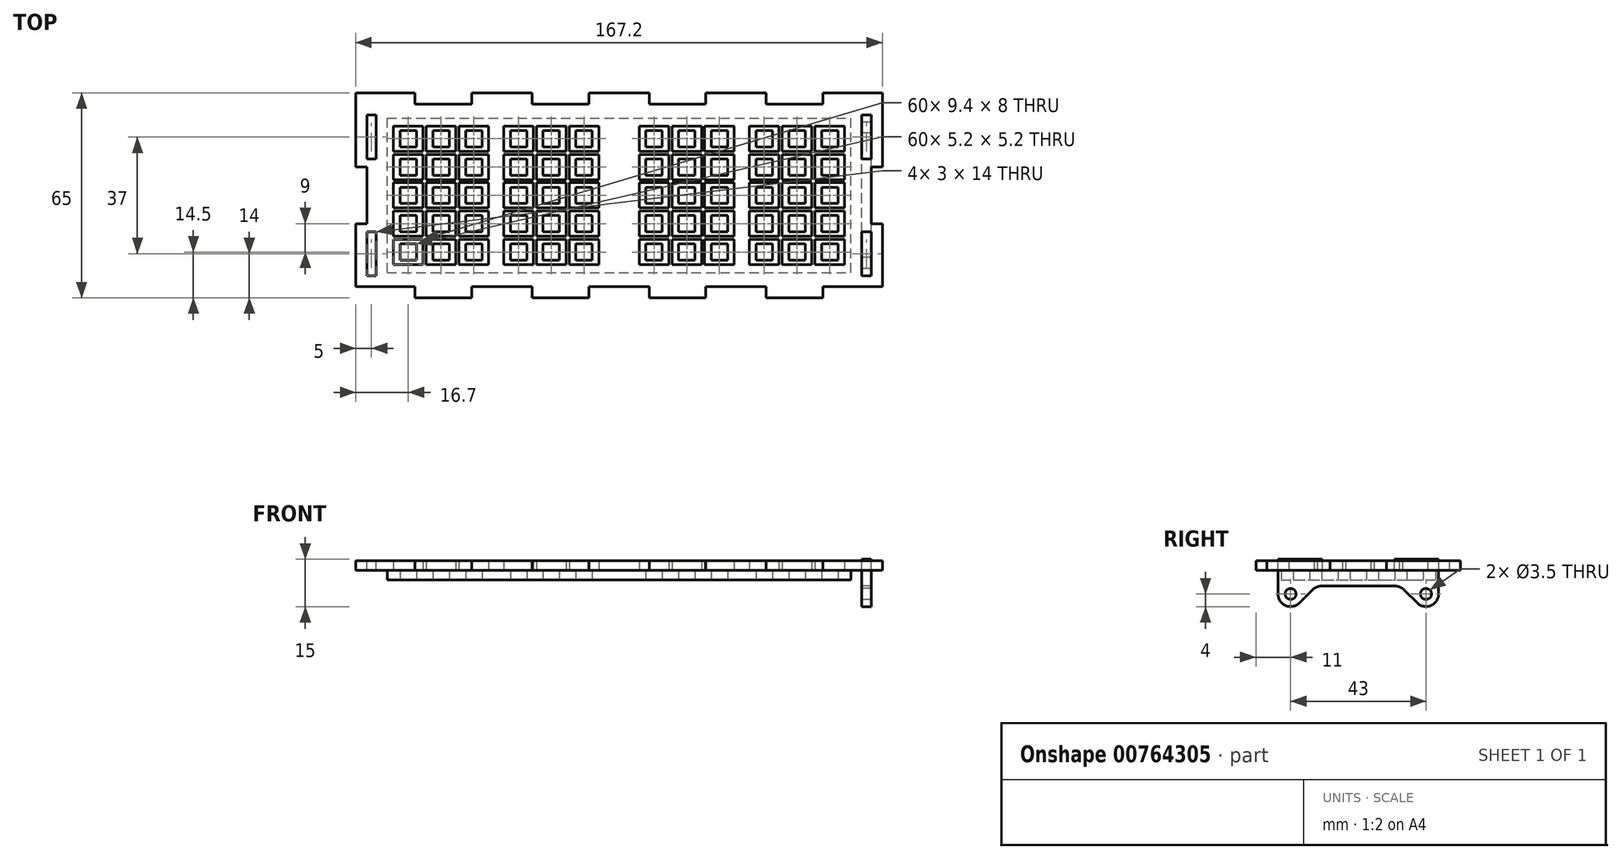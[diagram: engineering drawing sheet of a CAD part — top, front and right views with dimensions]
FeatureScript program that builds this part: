
annotation { "Feature Type Name" : "Feature", "Feature Type Description" : "" }
export const myFeature = defineFeature(function(context is Context, id is Id, definition is map)
    precondition{}
    {
        {
            var Q0;
            Q0=qCreatedBy(makeId("Top.planeOp"),FACE);
            var sketch = newSketch(context, id + "F0", { "sketchPlane" : qUnion([Q0])});
            skLineSegment(sketch, "E0.bottom", {"start": v(0, 0) * mm, "end": v(147.2, 0) * mm});
            skLineSegment(sketch, "E0.left", {"start": v(0, 0) * mm, "end": v(0, 49) * mm});
            skLineSegment(sketch, "E0.right", {"start": v(147.2, 0) * mm, "end": v(147.2, 49) * mm});
            skLineSegment(sketch, "E1.bottom", {"start": v(4.1, 3.9) * mm, "end": v(9.3, 3.9) * mm});
            skLineSegment(sketch, "E1.top", {"start": v(4.1, 9.1) * mm, "end": v(9.3, 9.1) * mm});
            skLineSegment(sketch, "E1.left", {"start": v(4.1, 3.9) * mm, "end": v(4.1, 9.1) * mm});
            skLineSegment(sketch, "E1.right", {"start": v(9.3, 3.9) * mm, "end": v(9.3, 9.1) * mm});
            skLineSegment(sketch, "E2.bottom", {"start": v(39.1, 3.9) * mm, "end": v(44.3, 3.9) * mm});
            skLineSegment(sketch, "E2.top", {"start": v(39.1, 9.1) * mm, "end": v(44.3, 9.1) * mm});
            skLineSegment(sketch, "E2.left", {"start": v(39.1, 3.9) * mm, "end": v(39.1, 9.1) * mm});
            skLineSegment(sketch, "E2.right", {"start": v(44.3, 3.9) * mm, "end": v(44.3, 9.1) * mm});
            skLineSegment(sketch, "E3", {"start": v(0, 49) * mm, "end": v(147.2, 49) * mm});
            skLineSegment(sketch, "E4.bottom", {"start": v(82.1, 3.9) * mm, "end": v(87.3, 3.9) * mm});
            skLineSegment(sketch, "E4.top", {"start": v(82.1, 9.1) * mm, "end": v(87.3, 9.1) * mm});
            skLineSegment(sketch, "E4.left", {"start": v(82.1, 3.9) * mm, "end": v(82.1, 9.1) * mm});
            skLineSegment(sketch, "E4.right", {"start": v(87.3, 3.9) * mm, "end": v(87.3, 9.1) * mm});
            skLineSegment(sketch, "E5.bottom", {"start": v(117.1, 3.9) * mm, "end": v(122.3, 3.9) * mm});
            skLineSegment(sketch, "E5.top", {"start": v(117.1, 9.1) * mm, "end": v(122.3, 9.1) * mm});
            skLineSegment(sketch, "E5.left", {"start": v(117.1, 3.9) * mm, "end": v(117.1, 9.1) * mm});
            skLineSegment(sketch, "E5.right", {"start": v(122.3, 3.9) * mm, "end": v(122.3, 9.1) * mm});
            skLineSegment(sketch, "E6.0.1.0", {"start": v(39.1, 12.9) * mm, "end": v(44.3, 12.9) * mm});
            skLineSegment(sketch, "E6.0.1.1", {"start": v(82.1, 12.9) * mm, "end": v(82.1, 18.1) * mm});
            skLineSegment(sketch, "E6.0.1.2", {"start": v(82.1, 18.1) * mm, "end": v(87.3, 18.1) * mm});
            skLineSegment(sketch, "E6.0.1.3", {"start": v(9.3, 12.9) * mm, "end": v(9.3, 18.1) * mm});
            skLineSegment(sketch, "E6.0.1.4", {"start": v(82.1, 12.9) * mm, "end": v(87.3, 12.9) * mm});
            skLineSegment(sketch, "E6.0.1.5", {"start": v(44.3, 12.9) * mm, "end": v(44.3, 18.1) * mm});
            skLineSegment(sketch, "E6.0.1.6", {"start": v(39.1, 12.9) * mm, "end": v(39.1, 18.1) * mm});
            skLineSegment(sketch, "E6.0.1.7", {"start": v(117.1, 12.9) * mm, "end": v(122.3, 12.9) * mm});
            skLineSegment(sketch, "E6.0.1.8", {"start": v(4.1, 12.9) * mm, "end": v(9.3, 12.9) * mm});
            skLineSegment(sketch, "E6.0.1.9", {"start": v(122.3, 12.9) * mm, "end": v(122.3, 18.1) * mm});
            skLineSegment(sketch, "E6.0.1.10", {"start": v(4.1, 12.9) * mm, "end": v(4.1, 18.1) * mm});
            skLineSegment(sketch, "E6.0.1.11", {"start": v(87.3, 12.9) * mm, "end": v(87.3, 18.1) * mm});
            skLineSegment(sketch, "E6.0.1.12", {"start": v(117.1, 12.9) * mm, "end": v(117.1, 18.1) * mm});
            skLineSegment(sketch, "E6.0.1.13", {"start": v(39.1, 18.1) * mm, "end": v(44.3, 18.1) * mm});
            skLineSegment(sketch, "E6.0.1.14", {"start": v(4.1, 18.1) * mm, "end": v(9.3, 18.1) * mm});
            skLineSegment(sketch, "E6.0.1.15", {"start": v(117.1, 18.1) * mm, "end": v(122.3, 18.1) * mm});
            skLineSegment(sketch, "E6.0.2.0", {"start": v(39.1, 21.9) * mm, "end": v(44.3, 21.9) * mm});
            skLineSegment(sketch, "E6.0.2.1", {"start": v(82.1, 21.9) * mm, "end": v(82.1, 27.1) * mm});
            skLineSegment(sketch, "E6.0.2.2", {"start": v(82.1, 27.1) * mm, "end": v(87.3, 27.1) * mm});
            skLineSegment(sketch, "E6.0.2.3", {"start": v(9.3, 21.9) * mm, "end": v(9.3, 27.1) * mm});
            skLineSegment(sketch, "E6.0.2.4", {"start": v(82.1, 21.9) * mm, "end": v(87.3, 21.9) * mm});
            skLineSegment(sketch, "E6.0.2.5", {"start": v(44.3, 21.9) * mm, "end": v(44.3, 27.1) * mm});
            skLineSegment(sketch, "E6.0.2.6", {"start": v(39.1, 21.9) * mm, "end": v(39.1, 27.1) * mm});
            skLineSegment(sketch, "E6.0.2.7", {"start": v(117.1, 21.9) * mm, "end": v(122.3, 21.9) * mm});
            skLineSegment(sketch, "E6.0.2.8", {"start": v(4.1, 21.9) * mm, "end": v(9.3, 21.9) * mm});
            skLineSegment(sketch, "E6.0.2.9", {"start": v(122.3, 21.9) * mm, "end": v(122.3, 27.1) * mm});
            skLineSegment(sketch, "E6.0.2.10", {"start": v(4.1, 21.9) * mm, "end": v(4.1, 27.1) * mm});
            skLineSegment(sketch, "E6.0.2.11", {"start": v(87.3, 21.9) * mm, "end": v(87.3, 27.1) * mm});
            skLineSegment(sketch, "E6.0.2.12", {"start": v(117.1, 21.9) * mm, "end": v(117.1, 27.1) * mm});
            skLineSegment(sketch, "E6.0.2.13", {"start": v(39.1, 27.1) * mm, "end": v(44.3, 27.1) * mm});
            skLineSegment(sketch, "E6.0.2.14", {"start": v(4.1, 27.1) * mm, "end": v(9.3, 27.1) * mm});
            skLineSegment(sketch, "E6.0.2.15", {"start": v(117.1, 27.1) * mm, "end": v(122.3, 27.1) * mm});
            skLineSegment(sketch, "E6.0.3.0", {"start": v(39.1, 30.9) * mm, "end": v(44.3, 30.9) * mm});
            skLineSegment(sketch, "E6.0.3.1", {"start": v(82.1, 30.9) * mm, "end": v(82.1, 36.1) * mm});
            skLineSegment(sketch, "E6.0.3.2", {"start": v(82.1, 36.1) * mm, "end": v(87.3, 36.1) * mm});
            skLineSegment(sketch, "E6.0.3.3", {"start": v(9.3, 30.9) * mm, "end": v(9.3, 36.1) * mm});
            skLineSegment(sketch, "E6.0.3.4", {"start": v(82.1, 30.9) * mm, "end": v(87.3, 30.9) * mm});
            skLineSegment(sketch, "E6.0.3.5", {"start": v(44.3, 30.9) * mm, "end": v(44.3, 36.1) * mm});
            skLineSegment(sketch, "E6.0.3.6", {"start": v(39.1, 30.9) * mm, "end": v(39.1, 36.1) * mm});
            skLineSegment(sketch, "E6.0.3.7", {"start": v(117.1, 30.9) * mm, "end": v(122.3, 30.9) * mm});
            skLineSegment(sketch, "E6.0.3.8", {"start": v(4.1, 30.9) * mm, "end": v(9.3, 30.9) * mm});
            skLineSegment(sketch, "E6.0.3.9", {"start": v(122.3, 30.9) * mm, "end": v(122.3, 36.1) * mm});
            skLineSegment(sketch, "E6.0.3.10", {"start": v(4.1, 30.9) * mm, "end": v(4.1, 36.1) * mm});
            skLineSegment(sketch, "E6.0.3.11", {"start": v(87.3, 30.9) * mm, "end": v(87.3, 36.1) * mm});
            skLineSegment(sketch, "E6.0.3.12", {"start": v(117.1, 30.9) * mm, "end": v(117.1, 36.1) * mm});
            skLineSegment(sketch, "E6.0.3.13", {"start": v(39.1, 36.1) * mm, "end": v(44.3, 36.1) * mm});
            skLineSegment(sketch, "E6.0.3.14", {"start": v(4.1, 36.1) * mm, "end": v(9.3, 36.1) * mm});
            skLineSegment(sketch, "E6.0.3.15", {"start": v(117.1, 36.1) * mm, "end": v(122.3, 36.1) * mm});
            skLineSegment(sketch, "E6.0.4.0", {"start": v(39.1, 39.9) * mm, "end": v(44.3, 39.9) * mm});
            skLineSegment(sketch, "E6.0.4.1", {"start": v(82.1, 39.9) * mm, "end": v(82.1, 45.1) * mm});
            skLineSegment(sketch, "E6.0.4.2", {"start": v(82.1, 45.1) * mm, "end": v(87.3, 45.1) * mm});
            skLineSegment(sketch, "E6.0.4.3", {"start": v(9.3, 39.9) * mm, "end": v(9.3, 45.1) * mm});
            skLineSegment(sketch, "E6.0.4.4", {"start": v(82.1, 39.9) * mm, "end": v(87.3, 39.9) * mm});
            skLineSegment(sketch, "E6.0.4.5", {"start": v(44.3, 39.9) * mm, "end": v(44.3, 45.1) * mm});
            skLineSegment(sketch, "E6.0.4.6", {"start": v(39.1, 39.9) * mm, "end": v(39.1, 45.1) * mm});
            skLineSegment(sketch, "E6.0.4.7", {"start": v(117.1, 39.9) * mm, "end": v(122.3, 39.9) * mm});
            skLineSegment(sketch, "E6.0.4.8", {"start": v(4.1, 39.9) * mm, "end": v(9.3, 39.9) * mm});
            skLineSegment(sketch, "E6.0.4.9", {"start": v(122.3, 39.9) * mm, "end": v(122.3, 45.1) * mm});
            skLineSegment(sketch, "E6.0.4.10", {"start": v(4.1, 39.9) * mm, "end": v(4.1, 45.1) * mm});
            skLineSegment(sketch, "E6.0.4.11", {"start": v(87.3, 39.9) * mm, "end": v(87.3, 45.1) * mm});
            skLineSegment(sketch, "E6.0.4.12", {"start": v(117.1, 39.9) * mm, "end": v(117.1, 45.1) * mm});
            skLineSegment(sketch, "E6.0.4.13", {"start": v(39.1, 45.1) * mm, "end": v(44.3, 45.1) * mm});
            skLineSegment(sketch, "E6.0.4.14", {"start": v(4.1, 45.1) * mm, "end": v(9.3, 45.1) * mm});
            skLineSegment(sketch, "E6.0.4.15", {"start": v(117.1, 45.1) * mm, "end": v(122.3, 45.1) * mm});
            skLineSegment(sketch, "E6.1.0.0", {"start": v(49.5, 3.9) * mm, "end": v(54.7, 3.9) * mm});
            skLineSegment(sketch, "E6.1.0.1", {"start": v(92.5, 3.9) * mm, "end": v(92.5, 9.1) * mm});
            skLineSegment(sketch, "E6.1.0.2", {"start": v(92.5, 9.1) * mm, "end": v(97.7, 9.1) * mm});
            skLineSegment(sketch, "E6.1.0.3", {"start": v(19.7, 3.9) * mm, "end": v(19.7, 9.1) * mm});
            skLineSegment(sketch, "E6.1.0.4", {"start": v(92.5, 3.9) * mm, "end": v(97.7, 3.9) * mm});
            skLineSegment(sketch, "E6.1.0.5", {"start": v(54.7, 3.9) * mm, "end": v(54.7, 9.1) * mm});
            skLineSegment(sketch, "E6.1.0.6", {"start": v(49.5, 3.9) * mm, "end": v(49.5, 9.1) * mm});
            skLineSegment(sketch, "E6.1.0.7", {"start": v(127.5, 3.9) * mm, "end": v(132.7, 3.9) * mm});
            skLineSegment(sketch, "E6.1.0.8", {"start": v(14.5, 3.9) * mm, "end": v(19.7, 3.9) * mm});
            skLineSegment(sketch, "E6.1.0.9", {"start": v(132.7, 3.9) * mm, "end": v(132.7, 9.1) * mm});
            skLineSegment(sketch, "E6.1.0.10", {"start": v(14.5, 3.9) * mm, "end": v(14.5, 9.1) * mm});
            skLineSegment(sketch, "E6.1.0.11", {"start": v(97.7, 3.9) * mm, "end": v(97.7, 9.1) * mm});
            skLineSegment(sketch, "E6.1.0.12", {"start": v(127.5, 3.9) * mm, "end": v(127.5, 9.1) * mm});
            skLineSegment(sketch, "E6.1.0.13", {"start": v(49.5, 9.1) * mm, "end": v(54.7, 9.1) * mm});
            skLineSegment(sketch, "E6.1.0.14", {"start": v(14.5, 9.1) * mm, "end": v(19.7, 9.1) * mm});
            skLineSegment(sketch, "E6.1.0.15", {"start": v(127.5, 9.1) * mm, "end": v(132.7, 9.1) * mm});
            skLineSegment(sketch, "E6.1.1.0", {"start": v(49.5, 12.9) * mm, "end": v(54.7, 12.9) * mm});
            skLineSegment(sketch, "E6.1.1.1", {"start": v(92.5, 12.9) * mm, "end": v(92.5, 18.1) * mm});
            skLineSegment(sketch, "E6.1.1.2", {"start": v(92.5, 18.1) * mm, "end": v(97.7, 18.1) * mm});
            skLineSegment(sketch, "E6.1.1.3", {"start": v(19.7, 12.9) * mm, "end": v(19.7, 18.1) * mm});
            skLineSegment(sketch, "E6.1.1.4", {"start": v(92.5, 12.9) * mm, "end": v(97.7, 12.9) * mm});
            skLineSegment(sketch, "E6.1.1.5", {"start": v(54.7, 12.9) * mm, "end": v(54.7, 18.1) * mm});
            skLineSegment(sketch, "E6.1.1.6", {"start": v(49.5, 12.9) * mm, "end": v(49.5, 18.1) * mm});
            skLineSegment(sketch, "E6.1.1.7", {"start": v(127.5, 12.9) * mm, "end": v(132.7, 12.9) * mm});
            skLineSegment(sketch, "E6.1.1.8", {"start": v(14.5, 12.9) * mm, "end": v(19.7, 12.9) * mm});
            skLineSegment(sketch, "E6.1.1.9", {"start": v(132.7, 12.9) * mm, "end": v(132.7, 18.1) * mm});
            skLineSegment(sketch, "E6.1.1.10", {"start": v(14.5, 12.9) * mm, "end": v(14.5, 18.1) * mm});
            skLineSegment(sketch, "E6.1.1.11", {"start": v(97.7, 12.9) * mm, "end": v(97.7, 18.1) * mm});
            skLineSegment(sketch, "E6.1.1.12", {"start": v(127.5, 12.9) * mm, "end": v(127.5, 18.1) * mm});
            skLineSegment(sketch, "E6.1.1.13", {"start": v(49.5, 18.1) * mm, "end": v(54.7, 18.1) * mm});
            skLineSegment(sketch, "E6.1.1.14", {"start": v(14.5, 18.1) * mm, "end": v(19.7, 18.1) * mm});
            skLineSegment(sketch, "E6.1.1.15", {"start": v(127.5, 18.1) * mm, "end": v(132.7, 18.1) * mm});
            skLineSegment(sketch, "E6.1.2.0", {"start": v(49.5, 21.9) * mm, "end": v(54.7, 21.9) * mm});
            skLineSegment(sketch, "E6.1.2.1", {"start": v(92.5, 21.9) * mm, "end": v(92.5, 27.1) * mm});
            skLineSegment(sketch, "E6.1.2.2", {"start": v(92.5, 27.1) * mm, "end": v(97.7, 27.1) * mm});
            skLineSegment(sketch, "E6.1.2.3", {"start": v(19.7, 21.9) * mm, "end": v(19.7, 27.1) * mm});
            skLineSegment(sketch, "E6.1.2.4", {"start": v(92.5, 21.9) * mm, "end": v(97.7, 21.9) * mm});
            skLineSegment(sketch, "E6.1.2.5", {"start": v(54.7, 21.9) * mm, "end": v(54.7, 27.1) * mm});
            skLineSegment(sketch, "E6.1.2.6", {"start": v(49.5, 21.9) * mm, "end": v(49.5, 27.1) * mm});
            skLineSegment(sketch, "E6.1.2.7", {"start": v(127.5, 21.9) * mm, "end": v(132.7, 21.9) * mm});
            skLineSegment(sketch, "E6.1.2.8", {"start": v(14.5, 21.9) * mm, "end": v(19.7, 21.9) * mm});
            skLineSegment(sketch, "E6.1.2.9", {"start": v(132.7, 21.9) * mm, "end": v(132.7, 27.1) * mm});
            skLineSegment(sketch, "E6.1.2.10", {"start": v(14.5, 21.9) * mm, "end": v(14.5, 27.1) * mm});
            skLineSegment(sketch, "E6.1.2.11", {"start": v(97.7, 21.9) * mm, "end": v(97.7, 27.1) * mm});
            skLineSegment(sketch, "E6.1.2.12", {"start": v(127.5, 21.9) * mm, "end": v(127.5, 27.1) * mm});
            skLineSegment(sketch, "E6.1.2.13", {"start": v(49.5, 27.1) * mm, "end": v(54.7, 27.1) * mm});
            skLineSegment(sketch, "E6.1.2.14", {"start": v(14.5, 27.1) * mm, "end": v(19.7, 27.1) * mm});
            skLineSegment(sketch, "E6.1.2.15", {"start": v(127.5, 27.1) * mm, "end": v(132.7, 27.1) * mm});
            skLineSegment(sketch, "E6.1.3.0", {"start": v(49.5, 30.9) * mm, "end": v(54.7, 30.9) * mm});
            skLineSegment(sketch, "E6.1.3.1", {"start": v(92.5, 30.9) * mm, "end": v(92.5, 36.1) * mm});
            skLineSegment(sketch, "E6.1.3.2", {"start": v(92.5, 36.1) * mm, "end": v(97.7, 36.1) * mm});
            skLineSegment(sketch, "E6.1.3.3", {"start": v(19.7, 30.9) * mm, "end": v(19.7, 36.1) * mm});
            skLineSegment(sketch, "E6.1.3.4", {"start": v(92.5, 30.9) * mm, "end": v(97.7, 30.9) * mm});
            skLineSegment(sketch, "E6.1.3.5", {"start": v(54.7, 30.9) * mm, "end": v(54.7, 36.1) * mm});
            skLineSegment(sketch, "E6.1.3.6", {"start": v(49.5, 30.9) * mm, "end": v(49.5, 36.1) * mm});
            skLineSegment(sketch, "E6.1.3.7", {"start": v(127.5, 30.9) * mm, "end": v(132.7, 30.9) * mm});
            skLineSegment(sketch, "E6.1.3.8", {"start": v(14.5, 30.9) * mm, "end": v(19.7, 30.9) * mm});
            skLineSegment(sketch, "E6.1.3.9", {"start": v(132.7, 30.9) * mm, "end": v(132.7, 36.1) * mm});
            skLineSegment(sketch, "E6.1.3.10", {"start": v(14.5, 30.9) * mm, "end": v(14.5, 36.1) * mm});
            skLineSegment(sketch, "E6.1.3.11", {"start": v(97.7, 30.9) * mm, "end": v(97.7, 36.1) * mm});
            skLineSegment(sketch, "E6.1.3.12", {"start": v(127.5, 30.9) * mm, "end": v(127.5, 36.1) * mm});
            skLineSegment(sketch, "E6.1.3.13", {"start": v(49.5, 36.1) * mm, "end": v(54.7, 36.1) * mm});
            skLineSegment(sketch, "E6.1.3.14", {"start": v(14.5, 36.1) * mm, "end": v(19.7, 36.1) * mm});
            skLineSegment(sketch, "E6.1.3.15", {"start": v(127.5, 36.1) * mm, "end": v(132.7, 36.1) * mm});
            skLineSegment(sketch, "E6.1.4.0", {"start": v(49.5, 39.9) * mm, "end": v(54.7, 39.9) * mm});
            skLineSegment(sketch, "E6.1.4.1", {"start": v(92.5, 39.9) * mm, "end": v(92.5, 45.1) * mm});
            skLineSegment(sketch, "E6.1.4.2", {"start": v(92.5, 45.1) * mm, "end": v(97.7, 45.1) * mm});
            skLineSegment(sketch, "E6.1.4.3", {"start": v(19.7, 39.9) * mm, "end": v(19.7, 45.1) * mm});
            skLineSegment(sketch, "E6.1.4.4", {"start": v(92.5, 39.9) * mm, "end": v(97.7, 39.9) * mm});
            skLineSegment(sketch, "E6.1.4.5", {"start": v(54.7, 39.9) * mm, "end": v(54.7, 45.1) * mm});
            skLineSegment(sketch, "E6.1.4.6", {"start": v(49.5, 39.9) * mm, "end": v(49.5, 45.1) * mm});
            skLineSegment(sketch, "E6.1.4.7", {"start": v(127.5, 39.9) * mm, "end": v(132.7, 39.9) * mm});
            skLineSegment(sketch, "E6.1.4.8", {"start": v(14.5, 39.9) * mm, "end": v(19.7, 39.9) * mm});
            skLineSegment(sketch, "E6.1.4.9", {"start": v(132.7, 39.9) * mm, "end": v(132.7, 45.1) * mm});
            skLineSegment(sketch, "E6.1.4.10", {"start": v(14.5, 39.9) * mm, "end": v(14.5, 45.1) * mm});
            skLineSegment(sketch, "E6.1.4.11", {"start": v(97.7, 39.9) * mm, "end": v(97.7, 45.1) * mm});
            skLineSegment(sketch, "E6.1.4.12", {"start": v(127.5, 39.9) * mm, "end": v(127.5, 45.1) * mm});
            skLineSegment(sketch, "E6.1.4.13", {"start": v(49.5, 45.1) * mm, "end": v(54.7, 45.1) * mm});
            skLineSegment(sketch, "E6.1.4.14", {"start": v(14.5, 45.1) * mm, "end": v(19.7, 45.1) * mm});
            skLineSegment(sketch, "E6.1.4.15", {"start": v(127.5, 45.1) * mm, "end": v(132.7, 45.1) * mm});
            skLineSegment(sketch, "E6.2.0.0", {"start": v(59.9, 3.9) * mm, "end": v(65.1, 3.9) * mm});
            skLineSegment(sketch, "E6.2.0.1", {"start": v(102.9, 3.9) * mm, "end": v(102.9, 9.1) * mm});
            skLineSegment(sketch, "E6.2.0.2", {"start": v(102.9, 9.1) * mm, "end": v(108.1, 9.1) * mm});
            skLineSegment(sketch, "E6.2.0.3", {"start": v(30.1, 3.9) * mm, "end": v(30.1, 9.1) * mm});
            skLineSegment(sketch, "E6.2.0.4", {"start": v(102.9, 3.9) * mm, "end": v(108.1, 3.9) * mm});
            skLineSegment(sketch, "E6.2.0.5", {"start": v(65.1, 3.9) * mm, "end": v(65.1, 9.1) * mm});
            skLineSegment(sketch, "E6.2.0.6", {"start": v(59.9, 3.9) * mm, "end": v(59.9, 9.1) * mm});
            skLineSegment(sketch, "E6.2.0.7", {"start": v(137.9, 3.9) * mm, "end": v(143.1, 3.9) * mm});
            skLineSegment(sketch, "E6.2.0.8", {"start": v(24.9, 3.9) * mm, "end": v(30.1, 3.9) * mm});
            skLineSegment(sketch, "E6.2.0.9", {"start": v(143.1, 3.9) * mm, "end": v(143.1, 9.1) * mm});
            skLineSegment(sketch, "E6.2.0.10", {"start": v(24.9, 3.9) * mm, "end": v(24.9, 9.1) * mm});
            skLineSegment(sketch, "E6.2.0.11", {"start": v(108.1, 3.9) * mm, "end": v(108.1, 9.1) * mm});
            skLineSegment(sketch, "E6.2.0.12", {"start": v(137.9, 3.9) * mm, "end": v(137.9, 9.1) * mm});
            skLineSegment(sketch, "E6.2.0.13", {"start": v(59.9, 9.1) * mm, "end": v(65.1, 9.1) * mm});
            skLineSegment(sketch, "E6.2.0.14", {"start": v(24.9, 9.1) * mm, "end": v(30.1, 9.1) * mm});
            skLineSegment(sketch, "E6.2.0.15", {"start": v(137.9, 9.1) * mm, "end": v(143.1, 9.1) * mm});
            skLineSegment(sketch, "E6.2.1.0", {"start": v(59.9, 12.9) * mm, "end": v(65.1, 12.9) * mm});
            skLineSegment(sketch, "E6.2.1.1", {"start": v(102.9, 12.9) * mm, "end": v(102.9, 18.1) * mm});
            skLineSegment(sketch, "E6.2.1.2", {"start": v(102.9, 18.1) * mm, "end": v(108.1, 18.1) * mm});
            skLineSegment(sketch, "E6.2.1.3", {"start": v(30.1, 12.9) * mm, "end": v(30.1, 18.1) * mm});
            skLineSegment(sketch, "E6.2.1.4", {"start": v(102.9, 12.9) * mm, "end": v(108.1, 12.9) * mm});
            skLineSegment(sketch, "E6.2.1.5", {"start": v(65.1, 12.9) * mm, "end": v(65.1, 18.1) * mm});
            skLineSegment(sketch, "E6.2.1.6", {"start": v(59.9, 12.9) * mm, "end": v(59.9, 18.1) * mm});
            skLineSegment(sketch, "E6.2.1.7", {"start": v(137.9, 12.9) * mm, "end": v(143.1, 12.9) * mm});
            skLineSegment(sketch, "E6.2.1.8", {"start": v(24.9, 12.9) * mm, "end": v(30.1, 12.9) * mm});
            skLineSegment(sketch, "E6.2.1.9", {"start": v(143.1, 12.9) * mm, "end": v(143.1, 18.1) * mm});
            skLineSegment(sketch, "E6.2.1.10", {"start": v(24.9, 12.9) * mm, "end": v(24.9, 18.1) * mm});
            skLineSegment(sketch, "E6.2.1.11", {"start": v(108.1, 12.9) * mm, "end": v(108.1, 18.1) * mm});
            skLineSegment(sketch, "E6.2.1.12", {"start": v(137.9, 12.9) * mm, "end": v(137.9, 18.1) * mm});
            skLineSegment(sketch, "E6.2.1.13", {"start": v(59.9, 18.1) * mm, "end": v(65.1, 18.1) * mm});
            skLineSegment(sketch, "E6.2.1.14", {"start": v(24.9, 18.1) * mm, "end": v(30.1, 18.1) * mm});
            skLineSegment(sketch, "E6.2.1.15", {"start": v(137.9, 18.1) * mm, "end": v(143.1, 18.1) * mm});
            skLineSegment(sketch, "E6.2.2.0", {"start": v(59.9, 21.9) * mm, "end": v(65.1, 21.9) * mm});
            skLineSegment(sketch, "E6.2.2.1", {"start": v(102.9, 21.9) * mm, "end": v(102.9, 27.1) * mm});
            skLineSegment(sketch, "E6.2.2.2", {"start": v(102.9, 27.1) * mm, "end": v(108.1, 27.1) * mm});
            skLineSegment(sketch, "E6.2.2.3", {"start": v(30.1, 21.9) * mm, "end": v(30.1, 27.1) * mm});
            skLineSegment(sketch, "E6.2.2.4", {"start": v(102.9, 21.9) * mm, "end": v(108.1, 21.9) * mm});
            skLineSegment(sketch, "E6.2.2.5", {"start": v(65.1, 21.9) * mm, "end": v(65.1, 27.1) * mm});
            skLineSegment(sketch, "E6.2.2.6", {"start": v(59.9, 21.9) * mm, "end": v(59.9, 27.1) * mm});
            skLineSegment(sketch, "E6.2.2.7", {"start": v(137.9, 21.9) * mm, "end": v(143.1, 21.9) * mm});
            skLineSegment(sketch, "E6.2.2.8", {"start": v(24.9, 21.9) * mm, "end": v(30.1, 21.9) * mm});
            skLineSegment(sketch, "E6.2.2.9", {"start": v(143.1, 21.9) * mm, "end": v(143.1, 27.1) * mm});
            skLineSegment(sketch, "E6.2.2.10", {"start": v(24.9, 21.9) * mm, "end": v(24.9, 27.1) * mm});
            skLineSegment(sketch, "E6.2.2.11", {"start": v(108.1, 21.9) * mm, "end": v(108.1, 27.1) * mm});
            skLineSegment(sketch, "E6.2.2.12", {"start": v(137.9, 21.9) * mm, "end": v(137.9, 27.1) * mm});
            skLineSegment(sketch, "E6.2.2.13", {"start": v(59.9, 27.1) * mm, "end": v(65.1, 27.1) * mm});
            skLineSegment(sketch, "E6.2.2.14", {"start": v(24.9, 27.1) * mm, "end": v(30.1, 27.1) * mm});
            skLineSegment(sketch, "E6.2.2.15", {"start": v(137.9, 27.1) * mm, "end": v(143.1, 27.1) * mm});
            skLineSegment(sketch, "E6.2.3.0", {"start": v(59.9, 30.9) * mm, "end": v(65.1, 30.9) * mm});
            skLineSegment(sketch, "E6.2.3.1", {"start": v(102.9, 30.9) * mm, "end": v(102.9, 36.1) * mm});
            skLineSegment(sketch, "E6.2.3.2", {"start": v(102.9, 36.1) * mm, "end": v(108.1, 36.1) * mm});
            skLineSegment(sketch, "E6.2.3.3", {"start": v(30.1, 30.9) * mm, "end": v(30.1, 36.1) * mm});
            skLineSegment(sketch, "E6.2.3.4", {"start": v(102.9, 30.9) * mm, "end": v(108.1, 30.9) * mm});
            skLineSegment(sketch, "E6.2.3.5", {"start": v(65.1, 30.9) * mm, "end": v(65.1, 36.1) * mm});
            skLineSegment(sketch, "E6.2.3.6", {"start": v(59.9, 30.9) * mm, "end": v(59.9, 36.1) * mm});
            skLineSegment(sketch, "E6.2.3.7", {"start": v(137.9, 30.9) * mm, "end": v(143.1, 30.9) * mm});
            skLineSegment(sketch, "E6.2.3.8", {"start": v(24.9, 30.9) * mm, "end": v(30.1, 30.9) * mm});
            skLineSegment(sketch, "E6.2.3.9", {"start": v(143.1, 30.9) * mm, "end": v(143.1, 36.1) * mm});
            skLineSegment(sketch, "E6.2.3.10", {"start": v(24.9, 30.9) * mm, "end": v(24.9, 36.1) * mm});
            skLineSegment(sketch, "E6.2.3.11", {"start": v(108.1, 30.9) * mm, "end": v(108.1, 36.1) * mm});
            skLineSegment(sketch, "E6.2.3.12", {"start": v(137.9, 30.9) * mm, "end": v(137.9, 36.1) * mm});
            skLineSegment(sketch, "E6.2.3.13", {"start": v(59.9, 36.1) * mm, "end": v(65.1, 36.1) * mm});
            skLineSegment(sketch, "E6.2.3.14", {"start": v(24.9, 36.1) * mm, "end": v(30.1, 36.1) * mm});
            skLineSegment(sketch, "E6.2.3.15", {"start": v(137.9, 36.1) * mm, "end": v(143.1, 36.1) * mm});
            skLineSegment(sketch, "E6.2.4.0", {"start": v(59.9, 39.9) * mm, "end": v(65.1, 39.9) * mm});
            skLineSegment(sketch, "E6.2.4.1", {"start": v(102.9, 39.9) * mm, "end": v(102.9, 45.1) * mm});
            skLineSegment(sketch, "E6.2.4.2", {"start": v(102.9, 45.1) * mm, "end": v(108.1, 45.1) * mm});
            skLineSegment(sketch, "E6.2.4.3", {"start": v(30.1, 39.9) * mm, "end": v(30.1, 45.1) * mm});
            skLineSegment(sketch, "E6.2.4.4", {"start": v(102.9, 39.9) * mm, "end": v(108.1, 39.9) * mm});
            skLineSegment(sketch, "E6.2.4.5", {"start": v(65.1, 39.9) * mm, "end": v(65.1, 45.1) * mm});
            skLineSegment(sketch, "E6.2.4.6", {"start": v(59.9, 39.9) * mm, "end": v(59.9, 45.1) * mm});
            skLineSegment(sketch, "E6.2.4.7", {"start": v(137.9, 39.9) * mm, "end": v(143.1, 39.9) * mm});
            skLineSegment(sketch, "E6.2.4.8", {"start": v(24.9, 39.9) * mm, "end": v(30.1, 39.9) * mm});
            skLineSegment(sketch, "E6.2.4.9", {"start": v(143.1, 39.9) * mm, "end": v(143.1, 45.1) * mm});
            skLineSegment(sketch, "E6.2.4.10", {"start": v(24.9, 39.9) * mm, "end": v(24.9, 45.1) * mm});
            skLineSegment(sketch, "E6.2.4.11", {"start": v(108.1, 39.9) * mm, "end": v(108.1, 45.1) * mm});
            skLineSegment(sketch, "E6.2.4.12", {"start": v(137.9, 39.9) * mm, "end": v(137.9, 45.1) * mm});
            skLineSegment(sketch, "E6.2.4.13", {"start": v(59.9, 45.1) * mm, "end": v(65.1, 45.1) * mm});
            skLineSegment(sketch, "E6.2.4.14", {"start": v(24.9, 45.1) * mm, "end": v(30.1, 45.1) * mm});
            skLineSegment(sketch, "E6.2.4.15", {"start": v(137.9, 45.1) * mm, "end": v(143.1, 45.1) * mm});
            skLineSegment(sketch, "E6.direction1", {"start": v(4.1, 3.9) * mm, "end": v(14.5, 3.9) * mm, "construction": true});
            skLineSegment(sketch, "E6.direction2", {"start": v(4.1, 3.9) * mm, "end": v(4.1, 12.9) * mm, "construction": true});
            skSolve(sketch);
        }
        {
            var Q0;
            Q0=makeQuery(id+"F0.imprint","IMPRINT",FACE,{"disambiguationData":[TD([[makeQuery(id+"F0.imprint","IMPRINT",EDGE,{"derivedFrom":sQuery(id+"F0.wireOp",EDGE,"E0.bottom")}),1.0]])]});
            extrude(context, id + "F1", {"entities" : qUnion([Q0]), "depth" : 3 * mm, "offsetDistance" : 25 * mm});
        }
        {
            var Q0;
            Q0=makeQuery(id+"F1.opExtrude","CAP_FACE",FACE,{"disambiguationData":[OSD([sQuery(id+"F0.wireOp",EDGE,"E0.bottom"),sQuery(id+"F0.wireOp",EDGE,"E0.top"),sQuery(id+"F0.wireOp",EDGE,"E0.left"),sQuery(id+"F0.wireOp",EDGE,"E0.right"),sQuery(id+"F0.wireOp",EDGE,"E1.bottom"),sQuery(id+"F0.wireOp",EDGE,"E1.top"),sQuery(id+"F0.wireOp",EDGE,"E1.left"),sQuery(id+"F0.wireOp",EDGE,"E1.right"),sQuery(id+"F0.wireOp",EDGE,"95869116-3487-4177-9028-07c310471c4a.0.1.0"),sQuery(id+"F0.wireOp",EDGE,"95869116-3487-4177-9028-07c310471c4a.0.1.1"),sQuery(id+"F0.wireOp",EDGE,"95869116-3487-4177-9028-07c310471c4a.0.1.2"),sQuery(id+"F0.wireOp",EDGE,"95869116-3487-4177-9028-07c310471c4a.0.1.3"),sQuery(id+"F0.wireOp",EDGE,"95869116-3487-4177-9028-07c310471c4a.0.2.0"),sQuery(id+"F0.wireOp",EDGE,"95869116-3487-4177-9028-07c310471c4a.0.2.1"),sQuery(id+"F0.wireOp",EDGE,"95869116-3487-4177-9028-07c310471c4a.0.2.2"),sQuery(id+"F0.wireOp",EDGE,"95869116-3487-4177-9028-07c310471c4a.0.2.3"),sQuery(id+"F0.wireOp",EDGE,"95869116-3487-4177-9028-07c310471c4a.0.3.0"),sQuery(id+"F0.wireOp",EDGE,"95869116-3487-4177-9028-07c310471c4a.0.3.1"),sQuery(id+"F0.wireOp",EDGE,"95869116-3487-4177-9028-07c310471c4a.0.3.2"),sQuery(id+"F0.wireOp",EDGE,"95869116-3487-4177-9028-07c310471c4a.0.3.3"),sQuery(id+"F0.wireOp",EDGE,"95869116-3487-4177-9028-07c310471c4a.0.4.0"),sQuery(id+"F0.wireOp",EDGE,"95869116-3487-4177-9028-07c310471c4a.0.4.1"),sQuery(id+"F0.wireOp",EDGE,"95869116-3487-4177-9028-07c310471c4a.0.4.2"),sQuery(id+"F0.wireOp",EDGE,"95869116-3487-4177-9028-07c310471c4a.0.4.3"),sQuery(id+"F0.wireOp",EDGE,"95869116-3487-4177-9028-07c310471c4a.1.0.0"),sQuery(id+"F0.wireOp",EDGE,"95869116-3487-4177-9028-07c310471c4a.1.0.1"),sQuery(id+"F0.wireOp",EDGE,"95869116-3487-4177-9028-07c310471c4a.1.0.2"),sQuery(id+"F0.wireOp",EDGE,"95869116-3487-4177-9028-07c310471c4a.1.0.3"),sQuery(id+"F0.wireOp",EDGE,"95869116-3487-4177-9028-07c310471c4a.1.1.0"),sQuery(id+"F0.wireOp",EDGE,"95869116-3487-4177-9028-07c310471c4a.1.1.1"),sQuery(id+"F0.wireOp",EDGE,"95869116-3487-4177-9028-07c310471c4a.1.1.2"),sQuery(id+"F0.wireOp",EDGE,"95869116-3487-4177-9028-07c310471c4a.1.1.3"),sQuery(id+"F0.wireOp",EDGE,"95869116-3487-4177-9028-07c310471c4a.1.2.0"),sQuery(id+"F0.wireOp",EDGE,"95869116-3487-4177-9028-07c310471c4a.1.2.1"),sQuery(id+"F0.wireOp",EDGE,"95869116-3487-4177-9028-07c310471c4a.1.2.2"),sQuery(id+"F0.wireOp",EDGE,"95869116-3487-4177-9028-07c310471c4a.1.2.3"),sQuery(id+"F0.wireOp",EDGE,"95869116-3487-4177-9028-07c310471c4a.1.3.0"),sQuery(id+"F0.wireOp",EDGE,"95869116-3487-4177-9028-07c310471c4a.1.3.1"),sQuery(id+"F0.wireOp",EDGE,"95869116-3487-4177-9028-07c310471c4a.1.3.2"),sQuery(id+"F0.wireOp",EDGE,"95869116-3487-4177-9028-07c310471c4a.1.3.3"),sQuery(id+"F0.wireOp",EDGE,"95869116-3487-4177-9028-07c310471c4a.1.4.0"),sQuery(id+"F0.wireOp",EDGE,"95869116-3487-4177-9028-07c310471c4a.1.4.1"),sQuery(id+"F0.wireOp",EDGE,"95869116-3487-4177-9028-07c310471c4a.1.4.2"),sQuery(id+"F0.wireOp",EDGE,"95869116-3487-4177-9028-07c310471c4a.1.4.3"),sQuery(id+"F0.wireOp",EDGE,"95869116-3487-4177-9028-07c310471c4a.2.0.0"),sQuery(id+"F0.wireOp",EDGE,"95869116-3487-4177-9028-07c310471c4a.2.0.1"),sQuery(id+"F0.wireOp",EDGE,"95869116-3487-4177-9028-07c310471c4a.2.0.2"),sQuery(id+"F0.wireOp",EDGE,"95869116-3487-4177-9028-07c310471c4a.2.0.3"),sQuery(id+"F0.wireOp",EDGE,"95869116-3487-4177-9028-07c310471c4a.2.1.0"),sQuery(id+"F0.wireOp",EDGE,"95869116-3487-4177-9028-07c310471c4a.2.1.1"),sQuery(id+"F0.wireOp",EDGE,"95869116-3487-4177-9028-07c310471c4a.2.1.2"),sQuery(id+"F0.wireOp",EDGE,"95869116-3487-4177-9028-07c310471c4a.2.1.3"),sQuery(id+"F0.wireOp",EDGE,"95869116-3487-4177-9028-07c310471c4a.2.2.0"),sQuery(id+"F0.wireOp",EDGE,"95869116-3487-4177-9028-07c310471c4a.2.2.1"),sQuery(id+"F0.wireOp",EDGE,"95869116-3487-4177-9028-07c310471c4a.2.2.2"),sQuery(id+"F0.wireOp",EDGE,"95869116-3487-4177-9028-07c310471c4a.2.2.3"),sQuery(id+"F0.wireOp",EDGE,"95869116-3487-4177-9028-07c310471c4a.2.3.0"),sQuery(id+"F0.wireOp",EDGE,"95869116-3487-4177-9028-07c310471c4a.2.3.1"),sQuery(id+"F0.wireOp",EDGE,"95869116-3487-4177-9028-07c310471c4a.2.3.2"),sQuery(id+"F0.wireOp",EDGE,"95869116-3487-4177-9028-07c310471c4a.2.3.3"),sQuery(id+"F0.wireOp",EDGE,"95869116-3487-4177-9028-07c310471c4a.2.4.0"),sQuery(id+"F0.wireOp",EDGE,"95869116-3487-4177-9028-07c310471c4a.2.4.1"),sQuery(id+"F0.wireOp",EDGE,"95869116-3487-4177-9028-07c310471c4a.2.4.2"),sQuery(id+"F0.wireOp",EDGE,"95869116-3487-4177-9028-07c310471c4a.2.4.3"),sQuery(id+"F0.wireOp",EDGE,"49dafa04-c45d-4b5c-802c-71c5818911b00.MirrorCS"),sQuery(id+"F0.wireOp",EDGE,"49dafa04-c45d-4b5c-802c-71c5818911b01.MirrorCS"),sQuery(id+"F0.wireOp",EDGE,"49dafa04-c45d-4b5c-802c-71c5818911b02.MirrorCS"),sQuery(id+"F0.wireOp",EDGE,"49dafa04-c45d-4b5c-802c-71c5818911b03.MirrorCS"),sQuery(id+"F0.wireOp",EDGE,"49dafa04-c45d-4b5c-802c-71c5818911b04.MirrorCS"),sQuery(id+"F0.wireOp",EDGE,"49dafa04-c45d-4b5c-802c-71c5818911b05.MirrorCS"),sQuery(id+"F0.wireOp",EDGE,"49dafa04-c45d-4b5c-802c-71c5818911b07.MirrorCS"),sQuery(id+"F0.wireOp",EDGE,"49dafa04-c45d-4b5c-802c-71c5818911b08.MirrorCS"),sQuery(id+"F0.wireOp",EDGE,"49dafa04-c45d-4b5c-802c-71c5818911b09.MirrorCS"),sQuery(id+"F0.wireOp",EDGE,"49dafa04-c45d-4b5c-802c-71c5818911b010.MirrorCS"),sQuery(id+"F0.wireOp",EDGE,"49dafa04-c45d-4b5c-802c-71c5818911b011.MirrorCS"),sQuery(id+"F0.wireOp",EDGE,"49dafa04-c45d-4b5c-802c-71c5818911b012.MirrorCS"),sQuery(id+"F0.wireOp",EDGE,"49dafa04-c45d-4b5c-802c-71c5818911b013.MirrorCS"),sQuery(id+"F0.wireOp",EDGE,"49dafa04-c45d-4b5c-802c-71c5818911b014.MirrorCS"),sQuery(id+"F0.wireOp",EDGE,"49dafa04-c45d-4b5c-802c-71c5818911b015.MirrorCS"),sQuery(id+"F0.wireOp",EDGE,"49dafa04-c45d-4b5c-802c-71c5818911b016.MirrorCS"),sQuery(id+"F0.wireOp",EDGE,"49dafa04-c45d-4b5c-802c-71c5818911b017.MirrorCS"),sQuery(id+"F0.wireOp",EDGE,"49dafa04-c45d-4b5c-802c-71c5818911b018.MirrorCS"),sQuery(id+"F0.wireOp",EDGE,"49dafa04-c45d-4b5c-802c-71c5818911b019.MirrorCS"),sQuery(id+"F0.wireOp",EDGE,"49dafa04-c45d-4b5c-802c-71c5818911b020.MirrorCS"),sQuery(id+"F0.wireOp",EDGE,"49dafa04-c45d-4b5c-802c-71c5818911b021.MirrorCS"),sQuery(id+"F0.wireOp",EDGE,"49dafa04-c45d-4b5c-802c-71c5818911b024.MirrorCS"),sQuery(id+"F0.wireOp",EDGE,"49dafa04-c45d-4b5c-802c-71c5818911b025.MirrorCS"),sQuery(id+"F0.wireOp",EDGE,"49dafa04-c45d-4b5c-802c-71c5818911b026.MirrorCS"),sQuery(id+"F0.wireOp",EDGE,"49dafa04-c45d-4b5c-802c-71c5818911b027.MirrorCS"),sQuery(id+"F0.wireOp",EDGE,"49dafa04-c45d-4b5c-802c-71c5818911b028.MirrorCS"),sQuery(id+"F0.wireOp",EDGE,"49dafa04-c45d-4b5c-802c-71c5818911b029.MirrorCS"),sQuery(id+"F0.wireOp",EDGE,"49dafa04-c45d-4b5c-802c-71c5818911b030.MirrorCS"),sQuery(id+"F0.wireOp",EDGE,"49dafa04-c45d-4b5c-802c-71c5818911b031.MirrorCS"),sQuery(id+"F0.wireOp",EDGE,"49dafa04-c45d-4b5c-802c-71c5818911b032.MirrorCS"),sQuery(id+"F0.wireOp",EDGE,"49dafa04-c45d-4b5c-802c-71c5818911b033.MirrorCS"),sQuery(id+"F0.wireOp",EDGE,"49dafa04-c45d-4b5c-802c-71c5818911b034.MirrorCS"),sQuery(id+"F0.wireOp",EDGE,"49dafa04-c45d-4b5c-802c-71c5818911b035.MirrorCS"),sQuery(id+"F0.wireOp",EDGE,"49dafa04-c45d-4b5c-802c-71c5818911b036.MirrorCS"),sQuery(id+"F0.wireOp",EDGE,"49dafa04-c45d-4b5c-802c-71c5818911b037.MirrorCS"),sQuery(id+"F0.wireOp",EDGE,"49dafa04-c45d-4b5c-802c-71c5818911b038.MirrorCS"),sQuery(id+"F0.wireOp",EDGE,"49dafa04-c45d-4b5c-802c-71c5818911b039.MirrorCS"),sQuery(id+"F0.wireOp",EDGE,"49dafa04-c45d-4b5c-802c-71c5818911b040.MirrorCS"),sQuery(id+"F0.wireOp",EDGE,"49dafa04-c45d-4b5c-802c-71c5818911b041.MirrorCS"),sQuery(id+"F0.wireOp",EDGE,"49dafa04-c45d-4b5c-802c-71c5818911b042.MirrorCS"),sQuery(id+"F0.wireOp",EDGE,"49dafa04-c45d-4b5c-802c-71c5818911b043.MirrorCS"),sQuery(id+"F0.wireOp",EDGE,"49dafa04-c45d-4b5c-802c-71c5818911b044.MirrorCS"),sQuery(id+"F0.wireOp",EDGE,"49dafa04-c45d-4b5c-802c-71c5818911b045.MirrorCS"),sQuery(id+"F0.wireOp",EDGE,"49dafa04-c45d-4b5c-802c-71c5818911b046.MirrorCS"),sQuery(id+"F0.wireOp",EDGE,"49dafa04-c45d-4b5c-802c-71c5818911b047.MirrorCS"),sQuery(id+"F0.wireOp",EDGE,"49dafa04-c45d-4b5c-802c-71c5818911b048.MirrorCS"),sQuery(id+"F0.wireOp",EDGE,"49dafa04-c45d-4b5c-802c-71c5818911b049.MirrorCS"),sQuery(id+"F0.wireOp",EDGE,"49dafa04-c45d-4b5c-802c-71c5818911b050.MirrorCS"),sQuery(id+"F0.wireOp",EDGE,"49dafa04-c45d-4b5c-802c-71c5818911b051.MirrorCS"),sQuery(id+"F0.wireOp",EDGE,"49dafa04-c45d-4b5c-802c-71c5818911b052.MirrorCS"),sQuery(id+"F0.wireOp",EDGE,"49dafa04-c45d-4b5c-802c-71c5818911b053.MirrorCS"),sQuery(id+"F0.wireOp",EDGE,"49dafa04-c45d-4b5c-802c-71c5818911b054.MirrorCS"),sQuery(id+"F0.wireOp",EDGE,"49dafa04-c45d-4b5c-802c-71c5818911b055.MirrorCS"),sQuery(id+"F0.wireOp",EDGE,"49dafa04-c45d-4b5c-802c-71c5818911b056.MirrorCS"),sQuery(id+"F0.wireOp",EDGE,"49dafa04-c45d-4b5c-802c-71c5818911b057.MirrorCS"),sQuery(id+"F0.wireOp",EDGE,"49dafa04-c45d-4b5c-802c-71c5818911b058.MirrorCS"),sQuery(id+"F0.wireOp",EDGE,"49dafa04-c45d-4b5c-802c-71c5818911b059.MirrorCS"),sQuery(id+"F0.wireOp",EDGE,"49dafa04-c45d-4b5c-802c-71c5818911b060.MirrorCS"),sQuery(id+"F0.wireOp",EDGE,"49dafa04-c45d-4b5c-802c-71c5818911b061.MirrorCS"),sQuery(id+"F0.wireOp",EDGE,"49dafa04-c45d-4b5c-802c-71c5818911b062.MirrorCS")])],"isStart":false});
            var sketch = newSketch(context, id + "F2", { "sketchPlane" : qUnion([Q0])});
            skLineSegment(sketch, "E7.bottom", {"start": v(-10, -8) * mm, "end": v(157.2, -8) * mm});
            skLineSegment(sketch, "E7.top", {"start": v(-10, 57) * mm, "end": v(157.2, 57) * mm});
            skLineSegment(sketch, "E7.left", {"start": v(-10, -8) * mm, "end": v(-10, 57) * mm});
            skLineSegment(sketch, "E7.right", {"start": v(157.2, -8) * mm, "end": v(157.2, 57) * mm});
            skLineSegment(sketch, "E8", {"start": v(73.6, -8) * mm, "end": v(73.6, 0) * mm, "construction": true});
            skLineSegment(sketch, "E9.bottom", {"start": v(2, 2.5) * mm, "end": v(11.4, 2.5) * mm});
            skLineSegment(sketch, "E9.top", {"start": v(2, 10.5) * mm, "end": v(11.4, 10.5) * mm});
            skLineSegment(sketch, "E9.left", {"start": v(2, 2.5) * mm, "end": v(2, 10.5) * mm});
            skLineSegment(sketch, "E9.right", {"start": v(11.4, 2.5) * mm, "end": v(11.4, 10.5) * mm});
            skLineSegment(sketch, "E10.bottom", {"start": v(37, 2.5) * mm, "end": v(46.4, 2.5) * mm});
            skLineSegment(sketch, "E10.top", {"start": v(37, 10.5) * mm, "end": v(46.4, 10.5) * mm});
            skLineSegment(sketch, "E10.left", {"start": v(37, 2.5) * mm, "end": v(37, 10.5) * mm});
            skLineSegment(sketch, "E10.right", {"start": v(46.4, 2.5) * mm, "end": v(46.4, 10.5) * mm});
            skLineSegment(sketch, "E11", {"start": v(6.7, 2.5) * mm, "end": v(6.7, 3.9) * mm, "construction": true});
            skLineSegment(sketch, "E12", {"start": v(2, 6.5) * mm, "end": v(4.1, 6.5) * mm, "construction": true});
            skLineSegment(sketch, "E13", {"start": v(41.7, 2.5) * mm, "end": v(41.7, 3.9) * mm, "construction": true});
            skPoint(sketch, "E13.startSnap0", {"position": v(41.7, 3.9) * mm});
            skPoint(sketch, "E13.startSnap1", {"position": v(41.7, 2.5) * mm});
            skLineSegment(sketch, "E14", {"start": v(37, 6.5) * mm, "end": v(39.1, 6.5) * mm, "construction": true});
            skLineSegment(sketch, "E15.bottom", {"start": v(80, 2.5) * mm, "end": v(89.4, 2.5) * mm});
            skLineSegment(sketch, "E15.top", {"start": v(80, 10.5) * mm, "end": v(89.4, 10.5) * mm});
            skLineSegment(sketch, "E15.left", {"start": v(80, 2.5) * mm, "end": v(80, 10.5) * mm});
            skLineSegment(sketch, "E15.right", {"start": v(89.4, 2.5) * mm, "end": v(89.4, 10.5) * mm});
            skLineSegment(sketch, "E16.bottom", {"start": v(115, 2.5) * mm, "end": v(124.4, 2.5) * mm});
            skLineSegment(sketch, "E16.top", {"start": v(115, 10.5) * mm, "end": v(124.4, 10.5) * mm});
            skLineSegment(sketch, "E16.left", {"start": v(115, 2.5) * mm, "end": v(115, 10.5) * mm});
            skLineSegment(sketch, "E16.right", {"start": v(124.4, 2.5) * mm, "end": v(124.4, 10.5) * mm});
            skLineSegment(sketch, "E17", {"start": v(84.7, 3.9) * mm, "end": v(84.7, 2.5) * mm, "construction": true});
            skLineSegment(sketch, "E18", {"start": v(82.1, 6.5) * mm, "end": v(80, 6.5) * mm, "construction": true});
            skLineSegment(sketch, "E19", {"start": v(119.7, 3.9) * mm, "end": v(119.7, 2.5) * mm, "construction": true});
            skLineSegment(sketch, "E20", {"start": v(115, 6.5) * mm, "end": v(117.1, 6.5) * mm, "construction": true});
            skLineSegment(sketch, "E21.0.1.0", {"start": v(115, 19.5) * mm, "end": v(124.4, 19.5) * mm});
            skLineSegment(sketch, "E21.0.1.1", {"start": v(115, 11.5) * mm, "end": v(115, 19.5) * mm});
            skLineSegment(sketch, "E21.0.1.2", {"start": v(115, 11.5) * mm, "end": v(124.4, 11.5) * mm});
            skLineSegment(sketch, "E21.0.1.3", {"start": v(124.4, 11.5) * mm, "end": v(124.4, 19.5) * mm});
            skLineSegment(sketch, "E21.0.1.4", {"start": v(89.4, 11.5) * mm, "end": v(89.4, 19.5) * mm});
            skLineSegment(sketch, "E21.0.1.5", {"start": v(80, 19.5) * mm, "end": v(89.4, 19.5) * mm});
            skLineSegment(sketch, "E21.0.1.6", {"start": v(80, 11.5) * mm, "end": v(80, 19.5) * mm});
            skLineSegment(sketch, "E21.0.1.7", {"start": v(80, 11.5) * mm, "end": v(89.4, 11.5) * mm});
            skLineSegment(sketch, "E21.0.1.8", {"start": v(37, 19.5) * mm, "end": v(46.4, 19.5) * mm});
            skLineSegment(sketch, "E21.0.1.9", {"start": v(37, 11.5) * mm, "end": v(37, 19.5) * mm});
            skLineSegment(sketch, "E21.0.1.10", {"start": v(37, 11.5) * mm, "end": v(46.4, 11.5) * mm});
            skLineSegment(sketch, "E21.0.1.11", {"start": v(46.4, 11.5) * mm, "end": v(46.4, 19.5) * mm});
            skLineSegment(sketch, "E21.0.1.12", {"start": v(2, 19.5) * mm, "end": v(11.4, 19.5) * mm});
            skLineSegment(sketch, "E21.0.1.13", {"start": v(2, 11.5) * mm, "end": v(2, 19.5) * mm});
            skLineSegment(sketch, "E21.0.1.14", {"start": v(2, 11.5) * mm, "end": v(11.4, 11.5) * mm});
            skLineSegment(sketch, "E21.0.1.15", {"start": v(11.4, 11.5) * mm, "end": v(11.4, 19.5) * mm});
            skLineSegment(sketch, "E21.0.2.0", {"start": v(115, 28.5) * mm, "end": v(124.4, 28.5) * mm});
            skLineSegment(sketch, "E21.0.2.1", {"start": v(115, 20.5) * mm, "end": v(115, 28.5) * mm});
            skLineSegment(sketch, "E21.0.2.2", {"start": v(115, 20.5) * mm, "end": v(124.4, 20.5) * mm});
            skLineSegment(sketch, "E21.0.2.3", {"start": v(124.4, 20.5) * mm, "end": v(124.4, 28.5) * mm});
            skLineSegment(sketch, "E21.0.2.4", {"start": v(89.4, 20.5) * mm, "end": v(89.4, 28.5) * mm});
            skLineSegment(sketch, "E21.0.2.5", {"start": v(80, 28.5) * mm, "end": v(89.4, 28.5) * mm});
            skLineSegment(sketch, "E21.0.2.6", {"start": v(80, 20.5) * mm, "end": v(80, 28.5) * mm});
            skLineSegment(sketch, "E21.0.2.7", {"start": v(80, 20.5) * mm, "end": v(89.4, 20.5) * mm});
            skLineSegment(sketch, "E21.0.2.8", {"start": v(37, 28.5) * mm, "end": v(46.4, 28.5) * mm});
            skLineSegment(sketch, "E21.0.2.9", {"start": v(37, 20.5) * mm, "end": v(37, 28.5) * mm});
            skLineSegment(sketch, "E21.0.2.10", {"start": v(37, 20.5) * mm, "end": v(46.4, 20.5) * mm});
            skLineSegment(sketch, "E21.0.2.11", {"start": v(46.4, 20.5) * mm, "end": v(46.4, 28.5) * mm});
            skLineSegment(sketch, "E21.0.2.12", {"start": v(2, 28.5) * mm, "end": v(11.4, 28.5) * mm});
            skLineSegment(sketch, "E21.0.2.13", {"start": v(2, 20.5) * mm, "end": v(2, 28.5) * mm});
            skLineSegment(sketch, "E21.0.2.14", {"start": v(2, 20.5) * mm, "end": v(11.4, 20.5) * mm});
            skLineSegment(sketch, "E21.0.2.15", {"start": v(11.4, 20.5) * mm, "end": v(11.4, 28.5) * mm});
            skLineSegment(sketch, "E21.0.3.0", {"start": v(115, 37.5) * mm, "end": v(124.4, 37.5) * mm});
            skLineSegment(sketch, "E21.0.3.1", {"start": v(115, 29.5) * mm, "end": v(115, 37.5) * mm});
            skLineSegment(sketch, "E21.0.3.2", {"start": v(115, 29.5) * mm, "end": v(124.4, 29.5) * mm});
            skLineSegment(sketch, "E21.0.3.3", {"start": v(124.4, 29.5) * mm, "end": v(124.4, 37.5) * mm});
            skLineSegment(sketch, "E21.0.3.4", {"start": v(89.4, 29.5) * mm, "end": v(89.4, 37.5) * mm});
            skLineSegment(sketch, "E21.0.3.5", {"start": v(80, 37.5) * mm, "end": v(89.4, 37.5) * mm});
            skLineSegment(sketch, "E21.0.3.6", {"start": v(80, 29.5) * mm, "end": v(80, 37.5) * mm});
            skLineSegment(sketch, "E21.0.3.7", {"start": v(80, 29.5) * mm, "end": v(89.4, 29.5) * mm});
            skLineSegment(sketch, "E21.0.3.8", {"start": v(37, 37.5) * mm, "end": v(46.4, 37.5) * mm});
            skLineSegment(sketch, "E21.0.3.9", {"start": v(37, 29.5) * mm, "end": v(37, 37.5) * mm});
            skLineSegment(sketch, "E21.0.3.10", {"start": v(37, 29.5) * mm, "end": v(46.4, 29.5) * mm});
            skLineSegment(sketch, "E21.0.3.11", {"start": v(46.4, 29.5) * mm, "end": v(46.4, 37.5) * mm});
            skLineSegment(sketch, "E21.0.3.12", {"start": v(2, 37.5) * mm, "end": v(11.4, 37.5) * mm});
            skLineSegment(sketch, "E21.0.3.13", {"start": v(2, 29.5) * mm, "end": v(2, 37.5) * mm});
            skLineSegment(sketch, "E21.0.3.14", {"start": v(2, 29.5) * mm, "end": v(11.4, 29.5) * mm});
            skLineSegment(sketch, "E21.0.3.15", {"start": v(11.4, 29.5) * mm, "end": v(11.4, 37.5) * mm});
            skLineSegment(sketch, "E21.0.4.0", {"start": v(115, 46.5) * mm, "end": v(124.4, 46.5) * mm});
            skLineSegment(sketch, "E21.0.4.1", {"start": v(115, 38.5) * mm, "end": v(115, 46.5) * mm});
            skLineSegment(sketch, "E21.0.4.2", {"start": v(115, 38.5) * mm, "end": v(124.4, 38.5) * mm});
            skLineSegment(sketch, "E21.0.4.3", {"start": v(124.4, 38.5) * mm, "end": v(124.4, 46.5) * mm});
            skLineSegment(sketch, "E21.0.4.4", {"start": v(89.4, 38.5) * mm, "end": v(89.4, 46.5) * mm});
            skLineSegment(sketch, "E21.0.4.5", {"start": v(80, 46.5) * mm, "end": v(89.4, 46.5) * mm});
            skLineSegment(sketch, "E21.0.4.6", {"start": v(80, 38.5) * mm, "end": v(80, 46.5) * mm});
            skLineSegment(sketch, "E21.0.4.7", {"start": v(80, 38.5) * mm, "end": v(89.4, 38.5) * mm});
            skLineSegment(sketch, "E21.0.4.8", {"start": v(37, 46.5) * mm, "end": v(46.4, 46.5) * mm});
            skLineSegment(sketch, "E21.0.4.9", {"start": v(37, 38.5) * mm, "end": v(37, 46.5) * mm});
            skLineSegment(sketch, "E21.0.4.10", {"start": v(37, 38.5) * mm, "end": v(46.4, 38.5) * mm});
            skLineSegment(sketch, "E21.0.4.11", {"start": v(46.4, 38.5) * mm, "end": v(46.4, 46.5) * mm});
            skLineSegment(sketch, "E21.0.4.12", {"start": v(2, 46.5) * mm, "end": v(11.4, 46.5) * mm});
            skLineSegment(sketch, "E21.0.4.13", {"start": v(2, 38.5) * mm, "end": v(2, 46.5) * mm});
            skLineSegment(sketch, "E21.0.4.14", {"start": v(2, 38.5) * mm, "end": v(11.4, 38.5) * mm});
            skLineSegment(sketch, "E21.0.4.15", {"start": v(11.4, 38.5) * mm, "end": v(11.4, 46.5) * mm});
            skLineSegment(sketch, "E21.1.0.0", {"start": v(125.4, 10.5) * mm, "end": v(134.8, 10.5) * mm});
            skLineSegment(sketch, "E21.1.0.1", {"start": v(125.4, 2.5) * mm, "end": v(125.4, 10.5) * mm});
            skLineSegment(sketch, "E21.1.0.2", {"start": v(125.4, 2.5) * mm, "end": v(134.8, 2.5) * mm});
            skLineSegment(sketch, "E21.1.0.3", {"start": v(134.8, 2.5) * mm, "end": v(134.8, 10.5) * mm});
            skLineSegment(sketch, "E21.1.0.4", {"start": v(99.8, 2.5) * mm, "end": v(99.8, 10.5) * mm});
            skLineSegment(sketch, "E21.1.0.5", {"start": v(90.4, 10.5) * mm, "end": v(99.8, 10.5) * mm});
            skLineSegment(sketch, "E21.1.0.6", {"start": v(90.4, 2.5) * mm, "end": v(90.4, 10.5) * mm});
            skLineSegment(sketch, "E21.1.0.7", {"start": v(90.4, 2.5) * mm, "end": v(99.8, 2.5) * mm});
            skLineSegment(sketch, "E21.1.0.8", {"start": v(47.4, 10.5) * mm, "end": v(56.8, 10.5) * mm});
            skLineSegment(sketch, "E21.1.0.9", {"start": v(47.4, 2.5) * mm, "end": v(47.4, 10.5) * mm});
            skLineSegment(sketch, "E21.1.0.10", {"start": v(47.4, 2.5) * mm, "end": v(56.8, 2.5) * mm});
            skLineSegment(sketch, "E21.1.0.11", {"start": v(56.8, 2.5) * mm, "end": v(56.8, 10.5) * mm});
            skLineSegment(sketch, "E21.1.0.12", {"start": v(12.4, 10.5) * mm, "end": v(21.8, 10.5) * mm});
            skLineSegment(sketch, "E21.1.0.13", {"start": v(12.4, 2.5) * mm, "end": v(12.4, 10.5) * mm});
            skLineSegment(sketch, "E21.1.0.14", {"start": v(12.4, 2.5) * mm, "end": v(21.8, 2.5) * mm});
            skLineSegment(sketch, "E21.1.0.15", {"start": v(21.8, 2.5) * mm, "end": v(21.8, 10.5) * mm});
            skLineSegment(sketch, "E21.1.1.0", {"start": v(125.4, 19.5) * mm, "end": v(134.8, 19.5) * mm});
            skLineSegment(sketch, "E21.1.1.1", {"start": v(125.4, 11.5) * mm, "end": v(125.4, 19.5) * mm});
            skLineSegment(sketch, "E21.1.1.2", {"start": v(125.4, 11.5) * mm, "end": v(134.8, 11.5) * mm});
            skLineSegment(sketch, "E21.1.1.3", {"start": v(134.8, 11.5) * mm, "end": v(134.8, 19.5) * mm});
            skLineSegment(sketch, "E21.1.1.4", {"start": v(99.8, 11.5) * mm, "end": v(99.8, 19.5) * mm});
            skLineSegment(sketch, "E21.1.1.5", {"start": v(90.4, 19.5) * mm, "end": v(99.8, 19.5) * mm});
            skLineSegment(sketch, "E21.1.1.6", {"start": v(90.4, 11.5) * mm, "end": v(90.4, 19.5) * mm});
            skLineSegment(sketch, "E21.1.1.7", {"start": v(90.4, 11.5) * mm, "end": v(99.8, 11.5) * mm});
            skLineSegment(sketch, "E21.1.1.8", {"start": v(47.4, 19.5) * mm, "end": v(56.8, 19.5) * mm});
            skLineSegment(sketch, "E21.1.1.9", {"start": v(47.4, 11.5) * mm, "end": v(47.4, 19.5) * mm});
            skLineSegment(sketch, "E21.1.1.10", {"start": v(47.4, 11.5) * mm, "end": v(56.8, 11.5) * mm});
            skLineSegment(sketch, "E21.1.1.11", {"start": v(56.8, 11.5) * mm, "end": v(56.8, 19.5) * mm});
            skLineSegment(sketch, "E21.1.1.12", {"start": v(12.4, 19.5) * mm, "end": v(21.8, 19.5) * mm});
            skLineSegment(sketch, "E21.1.1.13", {"start": v(12.4, 11.5) * mm, "end": v(12.4, 19.5) * mm});
            skLineSegment(sketch, "E21.1.1.14", {"start": v(12.4, 11.5) * mm, "end": v(21.8, 11.5) * mm});
            skLineSegment(sketch, "E21.1.1.15", {"start": v(21.8, 11.5) * mm, "end": v(21.8, 19.5) * mm});
            skLineSegment(sketch, "E21.1.2.0", {"start": v(125.4, 28.5) * mm, "end": v(134.8, 28.5) * mm});
            skLineSegment(sketch, "E21.1.2.1", {"start": v(125.4, 20.5) * mm, "end": v(125.4, 28.5) * mm});
            skLineSegment(sketch, "E21.1.2.2", {"start": v(125.4, 20.5) * mm, "end": v(134.8, 20.5) * mm});
            skLineSegment(sketch, "E21.1.2.3", {"start": v(134.8, 20.5) * mm, "end": v(134.8, 28.5) * mm});
            skLineSegment(sketch, "E21.1.2.4", {"start": v(99.8, 20.5) * mm, "end": v(99.8, 28.5) * mm});
            skLineSegment(sketch, "E21.1.2.5", {"start": v(90.4, 28.5) * mm, "end": v(99.8, 28.5) * mm});
            skLineSegment(sketch, "E21.1.2.6", {"start": v(90.4, 20.5) * mm, "end": v(90.4, 28.5) * mm});
            skLineSegment(sketch, "E21.1.2.7", {"start": v(90.4, 20.5) * mm, "end": v(99.8, 20.5) * mm});
            skLineSegment(sketch, "E21.1.2.8", {"start": v(47.4, 28.5) * mm, "end": v(56.8, 28.5) * mm});
            skLineSegment(sketch, "E21.1.2.9", {"start": v(47.4, 20.5) * mm, "end": v(47.4, 28.5) * mm});
            skLineSegment(sketch, "E21.1.2.10", {"start": v(47.4, 20.5) * mm, "end": v(56.8, 20.5) * mm});
            skLineSegment(sketch, "E21.1.2.11", {"start": v(56.8, 20.5) * mm, "end": v(56.8, 28.5) * mm});
            skLineSegment(sketch, "E21.1.2.12", {"start": v(12.4, 28.5) * mm, "end": v(21.8, 28.5) * mm});
            skLineSegment(sketch, "E21.1.2.13", {"start": v(12.4, 20.5) * mm, "end": v(12.4, 28.5) * mm});
            skLineSegment(sketch, "E21.1.2.14", {"start": v(12.4, 20.5) * mm, "end": v(21.8, 20.5) * mm});
            skLineSegment(sketch, "E21.1.2.15", {"start": v(21.8, 20.5) * mm, "end": v(21.8, 28.5) * mm});
            skLineSegment(sketch, "E21.1.3.0", {"start": v(125.4, 37.5) * mm, "end": v(134.8, 37.5) * mm});
            skLineSegment(sketch, "E21.1.3.1", {"start": v(125.4, 29.5) * mm, "end": v(125.4, 37.5) * mm});
            skLineSegment(sketch, "E21.1.3.2", {"start": v(125.4, 29.5) * mm, "end": v(134.8, 29.5) * mm});
            skLineSegment(sketch, "E21.1.3.3", {"start": v(134.8, 29.5) * mm, "end": v(134.8, 37.5) * mm});
            skLineSegment(sketch, "E21.1.3.4", {"start": v(99.8, 29.5) * mm, "end": v(99.8, 37.5) * mm});
            skLineSegment(sketch, "E21.1.3.5", {"start": v(90.4, 37.5) * mm, "end": v(99.8, 37.5) * mm});
            skLineSegment(sketch, "E21.1.3.6", {"start": v(90.4, 29.5) * mm, "end": v(90.4, 37.5) * mm});
            skLineSegment(sketch, "E21.1.3.7", {"start": v(90.4, 29.5) * mm, "end": v(99.8, 29.5) * mm});
            skLineSegment(sketch, "E21.1.3.8", {"start": v(47.4, 37.5) * mm, "end": v(56.8, 37.5) * mm});
            skLineSegment(sketch, "E21.1.3.9", {"start": v(47.4, 29.5) * mm, "end": v(47.4, 37.5) * mm});
            skLineSegment(sketch, "E21.1.3.10", {"start": v(47.4, 29.5) * mm, "end": v(56.8, 29.5) * mm});
            skLineSegment(sketch, "E21.1.3.11", {"start": v(56.8, 29.5) * mm, "end": v(56.8, 37.5) * mm});
            skLineSegment(sketch, "E21.1.3.12", {"start": v(12.4, 37.5) * mm, "end": v(21.8, 37.5) * mm});
            skLineSegment(sketch, "E21.1.3.13", {"start": v(12.4, 29.5) * mm, "end": v(12.4, 37.5) * mm});
            skLineSegment(sketch, "E21.1.3.14", {"start": v(12.4, 29.5) * mm, "end": v(21.8, 29.5) * mm});
            skLineSegment(sketch, "E21.1.3.15", {"start": v(21.8, 29.5) * mm, "end": v(21.8, 37.5) * mm});
            skLineSegment(sketch, "E21.1.4.0", {"start": v(125.4, 46.5) * mm, "end": v(134.8, 46.5) * mm});
            skLineSegment(sketch, "E21.1.4.1", {"start": v(125.4, 38.5) * mm, "end": v(125.4, 46.5) * mm});
            skLineSegment(sketch, "E21.1.4.2", {"start": v(125.4, 38.5) * mm, "end": v(134.8, 38.5) * mm});
            skLineSegment(sketch, "E21.1.4.3", {"start": v(134.8, 38.5) * mm, "end": v(134.8, 46.5) * mm});
            skLineSegment(sketch, "E21.1.4.4", {"start": v(99.8, 38.5) * mm, "end": v(99.8, 46.5) * mm});
            skLineSegment(sketch, "E21.1.4.5", {"start": v(90.4, 46.5) * mm, "end": v(99.8, 46.5) * mm});
            skLineSegment(sketch, "E21.1.4.6", {"start": v(90.4, 38.5) * mm, "end": v(90.4, 46.5) * mm});
            skLineSegment(sketch, "E21.1.4.7", {"start": v(90.4, 38.5) * mm, "end": v(99.8, 38.5) * mm});
            skLineSegment(sketch, "E21.1.4.8", {"start": v(47.4, 46.5) * mm, "end": v(56.8, 46.5) * mm});
            skLineSegment(sketch, "E21.1.4.9", {"start": v(47.4, 38.5) * mm, "end": v(47.4, 46.5) * mm});
            skLineSegment(sketch, "E21.1.4.10", {"start": v(47.4, 38.5) * mm, "end": v(56.8, 38.5) * mm});
            skLineSegment(sketch, "E21.1.4.11", {"start": v(56.8, 38.5) * mm, "end": v(56.8, 46.5) * mm});
            skLineSegment(sketch, "E21.1.4.12", {"start": v(12.4, 46.5) * mm, "end": v(21.8, 46.5) * mm});
            skLineSegment(sketch, "E21.1.4.13", {"start": v(12.4, 38.5) * mm, "end": v(12.4, 46.5) * mm});
            skLineSegment(sketch, "E21.1.4.14", {"start": v(12.4, 38.5) * mm, "end": v(21.8, 38.5) * mm});
            skLineSegment(sketch, "E21.1.4.15", {"start": v(21.8, 38.5) * mm, "end": v(21.8, 46.5) * mm});
            skLineSegment(sketch, "E21.2.0.0", {"start": v(135.8, 10.5) * mm, "end": v(145.2, 10.5) * mm});
            skLineSegment(sketch, "E21.2.0.1", {"start": v(135.8, 2.5) * mm, "end": v(135.8, 10.5) * mm});
            skLineSegment(sketch, "E21.2.0.2", {"start": v(135.8, 2.5) * mm, "end": v(145.2, 2.5) * mm});
            skLineSegment(sketch, "E21.2.0.3", {"start": v(145.2, 2.5) * mm, "end": v(145.2, 10.5) * mm});
            skLineSegment(sketch, "E21.2.0.4", {"start": v(110.2, 2.5) * mm, "end": v(110.2, 10.5) * mm});
            skLineSegment(sketch, "E21.2.0.5", {"start": v(100.8, 10.5) * mm, "end": v(110.2, 10.5) * mm});
            skLineSegment(sketch, "E21.2.0.6", {"start": v(100.8, 2.5) * mm, "end": v(100.8, 10.5) * mm});
            skLineSegment(sketch, "E21.2.0.7", {"start": v(100.8, 2.5) * mm, "end": v(110.2, 2.5) * mm});
            skLineSegment(sketch, "E21.2.0.8", {"start": v(57.8, 10.5) * mm, "end": v(67.2, 10.5) * mm});
            skLineSegment(sketch, "E21.2.0.9", {"start": v(57.8, 2.5) * mm, "end": v(57.8, 10.5) * mm});
            skLineSegment(sketch, "E21.2.0.10", {"start": v(57.8, 2.5) * mm, "end": v(67.2, 2.5) * mm});
            skLineSegment(sketch, "E21.2.0.11", {"start": v(67.2, 2.5) * mm, "end": v(67.2, 10.5) * mm});
            skLineSegment(sketch, "E21.2.0.12", {"start": v(22.8, 10.5) * mm, "end": v(32.2, 10.5) * mm});
            skLineSegment(sketch, "E21.2.0.13", {"start": v(22.8, 2.5) * mm, "end": v(22.8, 10.5) * mm});
            skLineSegment(sketch, "E21.2.0.14", {"start": v(22.8, 2.5) * mm, "end": v(32.2, 2.5) * mm});
            skLineSegment(sketch, "E21.2.0.15", {"start": v(32.2, 2.5) * mm, "end": v(32.2, 10.5) * mm});
            skLineSegment(sketch, "E21.2.1.0", {"start": v(135.8, 19.5) * mm, "end": v(145.2, 19.5) * mm});
            skLineSegment(sketch, "E21.2.1.1", {"start": v(135.8, 11.5) * mm, "end": v(135.8, 19.5) * mm});
            skLineSegment(sketch, "E21.2.1.2", {"start": v(135.8, 11.5) * mm, "end": v(145.2, 11.5) * mm});
            skLineSegment(sketch, "E21.2.1.3", {"start": v(145.2, 11.5) * mm, "end": v(145.2, 19.5) * mm});
            skLineSegment(sketch, "E21.2.1.4", {"start": v(110.2, 11.5) * mm, "end": v(110.2, 19.5) * mm});
            skLineSegment(sketch, "E21.2.1.5", {"start": v(100.8, 19.5) * mm, "end": v(110.2, 19.5) * mm});
            skLineSegment(sketch, "E21.2.1.6", {"start": v(100.8, 11.5) * mm, "end": v(100.8, 19.5) * mm});
            skLineSegment(sketch, "E21.2.1.7", {"start": v(100.8, 11.5) * mm, "end": v(110.2, 11.5) * mm});
            skLineSegment(sketch, "E21.2.1.8", {"start": v(57.8, 19.5) * mm, "end": v(67.2, 19.5) * mm});
            skLineSegment(sketch, "E21.2.1.9", {"start": v(57.8, 11.5) * mm, "end": v(57.8, 19.5) * mm});
            skLineSegment(sketch, "E21.2.1.10", {"start": v(57.8, 11.5) * mm, "end": v(67.2, 11.5) * mm});
            skLineSegment(sketch, "E21.2.1.11", {"start": v(67.2, 11.5) * mm, "end": v(67.2, 19.5) * mm});
            skLineSegment(sketch, "E21.2.1.12", {"start": v(22.8, 19.5) * mm, "end": v(32.2, 19.5) * mm});
            skLineSegment(sketch, "E21.2.1.13", {"start": v(22.8, 11.5) * mm, "end": v(22.8, 19.5) * mm});
            skLineSegment(sketch, "E21.2.1.14", {"start": v(22.8, 11.5) * mm, "end": v(32.2, 11.5) * mm});
            skLineSegment(sketch, "E21.2.1.15", {"start": v(32.2, 11.5) * mm, "end": v(32.2, 19.5) * mm});
            skLineSegment(sketch, "E21.2.2.0", {"start": v(135.8, 28.5) * mm, "end": v(145.2, 28.5) * mm});
            skLineSegment(sketch, "E21.2.2.1", {"start": v(135.8, 20.5) * mm, "end": v(135.8, 28.5) * mm});
            skLineSegment(sketch, "E21.2.2.2", {"start": v(135.8, 20.5) * mm, "end": v(145.2, 20.5) * mm});
            skLineSegment(sketch, "E21.2.2.3", {"start": v(145.2, 20.5) * mm, "end": v(145.2, 28.5) * mm});
            skLineSegment(sketch, "E21.2.2.4", {"start": v(110.2, 20.5) * mm, "end": v(110.2, 28.5) * mm});
            skLineSegment(sketch, "E21.2.2.5", {"start": v(100.8, 28.5) * mm, "end": v(110.2, 28.5) * mm});
            skLineSegment(sketch, "E21.2.2.6", {"start": v(100.8, 20.5) * mm, "end": v(100.8, 28.5) * mm});
            skLineSegment(sketch, "E21.2.2.7", {"start": v(100.8, 20.5) * mm, "end": v(110.2, 20.5) * mm});
            skLineSegment(sketch, "E21.2.2.8", {"start": v(57.8, 28.5) * mm, "end": v(67.2, 28.5) * mm});
            skLineSegment(sketch, "E21.2.2.9", {"start": v(57.8, 20.5) * mm, "end": v(57.8, 28.5) * mm});
            skLineSegment(sketch, "E21.2.2.10", {"start": v(57.8, 20.5) * mm, "end": v(67.2, 20.5) * mm});
            skLineSegment(sketch, "E21.2.2.11", {"start": v(67.2, 20.5) * mm, "end": v(67.2, 28.5) * mm});
            skLineSegment(sketch, "E21.2.2.12", {"start": v(22.8, 28.5) * mm, "end": v(32.2, 28.5) * mm});
            skLineSegment(sketch, "E21.2.2.13", {"start": v(22.8, 20.5) * mm, "end": v(22.8, 28.5) * mm});
            skLineSegment(sketch, "E21.2.2.14", {"start": v(22.8, 20.5) * mm, "end": v(32.2, 20.5) * mm});
            skLineSegment(sketch, "E21.2.2.15", {"start": v(32.2, 20.5) * mm, "end": v(32.2, 28.5) * mm});
            skLineSegment(sketch, "E21.2.3.0", {"start": v(135.8, 37.5) * mm, "end": v(145.2, 37.5) * mm});
            skLineSegment(sketch, "E21.2.3.1", {"start": v(135.8, 29.5) * mm, "end": v(135.8, 37.5) * mm});
            skLineSegment(sketch, "E21.2.3.2", {"start": v(135.8, 29.5) * mm, "end": v(145.2, 29.5) * mm});
            skLineSegment(sketch, "E21.2.3.3", {"start": v(145.2, 29.5) * mm, "end": v(145.2, 37.5) * mm});
            skLineSegment(sketch, "E21.2.3.4", {"start": v(110.2, 29.5) * mm, "end": v(110.2, 37.5) * mm});
            skLineSegment(sketch, "E21.2.3.5", {"start": v(100.8, 37.5) * mm, "end": v(110.2, 37.5) * mm});
            skLineSegment(sketch, "E21.2.3.6", {"start": v(100.8, 29.5) * mm, "end": v(100.8, 37.5) * mm});
            skLineSegment(sketch, "E21.2.3.7", {"start": v(100.8, 29.5) * mm, "end": v(110.2, 29.5) * mm});
            skLineSegment(sketch, "E21.2.3.8", {"start": v(57.8, 37.5) * mm, "end": v(67.2, 37.5) * mm});
            skLineSegment(sketch, "E21.2.3.9", {"start": v(57.8, 29.5) * mm, "end": v(57.8, 37.5) * mm});
            skLineSegment(sketch, "E21.2.3.10", {"start": v(57.8, 29.5) * mm, "end": v(67.2, 29.5) * mm});
            skLineSegment(sketch, "E21.2.3.11", {"start": v(67.2, 29.5) * mm, "end": v(67.2, 37.5) * mm});
            skLineSegment(sketch, "E21.2.3.12", {"start": v(22.8, 37.5) * mm, "end": v(32.2, 37.5) * mm});
            skLineSegment(sketch, "E21.2.3.13", {"start": v(22.8, 29.5) * mm, "end": v(22.8, 37.5) * mm});
            skLineSegment(sketch, "E21.2.3.14", {"start": v(22.8, 29.5) * mm, "end": v(32.2, 29.5) * mm});
            skLineSegment(sketch, "E21.2.3.15", {"start": v(32.2, 29.5) * mm, "end": v(32.2, 37.5) * mm});
            skLineSegment(sketch, "E21.2.4.0", {"start": v(135.8, 46.5) * mm, "end": v(145.2, 46.5) * mm});
            skLineSegment(sketch, "E21.2.4.1", {"start": v(135.8, 38.5) * mm, "end": v(135.8, 46.5) * mm});
            skLineSegment(sketch, "E21.2.4.2", {"start": v(135.8, 38.5) * mm, "end": v(145.2, 38.5) * mm});
            skLineSegment(sketch, "E21.2.4.3", {"start": v(145.2, 38.5) * mm, "end": v(145.2, 46.5) * mm});
            skLineSegment(sketch, "E21.2.4.4", {"start": v(110.2, 38.5) * mm, "end": v(110.2, 46.5) * mm});
            skLineSegment(sketch, "E21.2.4.5", {"start": v(100.8, 46.5) * mm, "end": v(110.2, 46.5) * mm});
            skLineSegment(sketch, "E21.2.4.6", {"start": v(100.8, 38.5) * mm, "end": v(100.8, 46.5) * mm});
            skLineSegment(sketch, "E21.2.4.7", {"start": v(100.8, 38.5) * mm, "end": v(110.2, 38.5) * mm});
            skLineSegment(sketch, "E21.2.4.8", {"start": v(57.8, 46.5) * mm, "end": v(67.2, 46.5) * mm});
            skLineSegment(sketch, "E21.2.4.9", {"start": v(57.8, 38.5) * mm, "end": v(57.8, 46.5) * mm});
            skLineSegment(sketch, "E21.2.4.10", {"start": v(57.8, 38.5) * mm, "end": v(67.2, 38.5) * mm});
            skLineSegment(sketch, "E21.2.4.11", {"start": v(67.2, 38.5) * mm, "end": v(67.2, 46.5) * mm});
            skLineSegment(sketch, "E21.2.4.12", {"start": v(22.8, 46.5) * mm, "end": v(32.2, 46.5) * mm});
            skLineSegment(sketch, "E21.2.4.13", {"start": v(22.8, 38.5) * mm, "end": v(22.8, 46.5) * mm});
            skLineSegment(sketch, "E21.2.4.14", {"start": v(22.8, 38.5) * mm, "end": v(32.2, 38.5) * mm});
            skLineSegment(sketch, "E21.2.4.15", {"start": v(32.2, 38.5) * mm, "end": v(32.2, 46.5) * mm});
            skLineSegment(sketch, "E21.direction1", {"start": v(2, 2.5) * mm, "end": v(12.4, 2.5) * mm, "construction": true});
            skLineSegment(sketch, "E21.direction2", {"start": v(2, 2.5) * mm, "end": v(2, 11.5) * mm, "construction": true});
            skLineSegment(sketch, "E22", {"start": v(0, 24.5) * mm, "end": v(-10, 24.5) * mm, "construction": true});
            skSolve(sketch);
        }
        {
            var Q0;
            Q0 = qSketchRegion(id + "F2", true);
            extrude(context, id + "F3", {"entities" : qUnion([Q0]), "depth" : 3 * mm, "offsetDistance" : 25 * mm});
        }
        {
            var Q0;
            Q0=makeQuery(id+"F3.opExtrude","CAP_FACE",FACE,{"disambiguationData":[OSD([sQuery(id+"F2.wireOp",EDGE,"E7.bottom"),sQuery(id+"F2.wireOp",EDGE,"E7.top"),sQuery(id+"F2.wireOp",EDGE,"E7.left"),sQuery(id+"F2.wireOp",EDGE,"E7.right"),sQuery(id+"F2.wireOp",EDGE,"E9.bottom"),sQuery(id+"F2.wireOp",EDGE,"E9.top"),sQuery(id+"F2.wireOp",EDGE,"E9.left"),sQuery(id+"F2.wireOp",EDGE,"E9.right"),sQuery(id+"F2.wireOp",EDGE,"E10.bottom"),sQuery(id+"F2.wireOp",EDGE,"E10.top"),sQuery(id+"F2.wireOp",EDGE,"E10.left"),sQuery(id+"F2.wireOp",EDGE,"E10.right"),sQuery(id+"F2.wireOp",EDGE,"E15.bottom"),sQuery(id+"F2.wireOp",EDGE,"E15.top"),sQuery(id+"F2.wireOp",EDGE,"E15.left"),sQuery(id+"F2.wireOp",EDGE,"E15.right"),sQuery(id+"F2.wireOp",EDGE,"E16.bottom"),sQuery(id+"F2.wireOp",EDGE,"E16.top"),sQuery(id+"F2.wireOp",EDGE,"E16.left"),sQuery(id+"F2.wireOp",EDGE,"E16.right"),sQuery(id+"F2.wireOp",EDGE,"E21.0.1.0"),sQuery(id+"F2.wireOp",EDGE,"E21.0.1.1"),sQuery(id+"F2.wireOp",EDGE,"E21.0.1.2"),sQuery(id+"F2.wireOp",EDGE,"E21.0.1.3"),sQuery(id+"F2.wireOp",EDGE,"E21.0.1.4"),sQuery(id+"F2.wireOp",EDGE,"E21.0.1.5"),sQuery(id+"F2.wireOp",EDGE,"E21.0.1.6"),sQuery(id+"F2.wireOp",EDGE,"E21.0.1.7"),sQuery(id+"F2.wireOp",EDGE,"E21.0.1.8"),sQuery(id+"F2.wireOp",EDGE,"E21.0.1.9"),sQuery(id+"F2.wireOp",EDGE,"E21.0.1.10"),sQuery(id+"F2.wireOp",EDGE,"E21.0.1.11"),sQuery(id+"F2.wireOp",EDGE,"E21.0.1.12"),sQuery(id+"F2.wireOp",EDGE,"E21.0.1.13"),sQuery(id+"F2.wireOp",EDGE,"E21.0.1.14"),sQuery(id+"F2.wireOp",EDGE,"E21.0.1.15"),sQuery(id+"F2.wireOp",EDGE,"E21.0.2.0"),sQuery(id+"F2.wireOp",EDGE,"E21.0.2.1"),sQuery(id+"F2.wireOp",EDGE,"E21.0.2.2"),sQuery(id+"F2.wireOp",EDGE,"E21.0.2.3"),sQuery(id+"F2.wireOp",EDGE,"E21.0.2.4"),sQuery(id+"F2.wireOp",EDGE,"E21.0.2.5"),sQuery(id+"F2.wireOp",EDGE,"E21.0.2.6"),sQuery(id+"F2.wireOp",EDGE,"E21.0.2.7"),sQuery(id+"F2.wireOp",EDGE,"E21.0.2.8"),sQuery(id+"F2.wireOp",EDGE,"E21.0.2.9"),sQuery(id+"F2.wireOp",EDGE,"E21.0.2.10"),sQuery(id+"F2.wireOp",EDGE,"E21.0.2.11"),sQuery(id+"F2.wireOp",EDGE,"E21.0.2.12"),sQuery(id+"F2.wireOp",EDGE,"E21.0.2.13"),sQuery(id+"F2.wireOp",EDGE,"E21.0.2.14"),sQuery(id+"F2.wireOp",EDGE,"E21.0.2.15"),sQuery(id+"F2.wireOp",EDGE,"E21.0.3.0"),sQuery(id+"F2.wireOp",EDGE,"E21.0.3.1"),sQuery(id+"F2.wireOp",EDGE,"E21.0.3.2"),sQuery(id+"F2.wireOp",EDGE,"E21.0.3.3"),sQuery(id+"F2.wireOp",EDGE,"E21.0.3.4"),sQuery(id+"F2.wireOp",EDGE,"E21.0.3.5"),sQuery(id+"F2.wireOp",EDGE,"E21.0.3.6"),sQuery(id+"F2.wireOp",EDGE,"E21.0.3.7"),sQuery(id+"F2.wireOp",EDGE,"E21.0.3.8"),sQuery(id+"F2.wireOp",EDGE,"E21.0.3.9"),sQuery(id+"F2.wireOp",EDGE,"E21.0.3.10"),sQuery(id+"F2.wireOp",EDGE,"E21.0.3.11"),sQuery(id+"F2.wireOp",EDGE,"E21.0.3.12"),sQuery(id+"F2.wireOp",EDGE,"E21.0.3.13"),sQuery(id+"F2.wireOp",EDGE,"E21.0.3.14"),sQuery(id+"F2.wireOp",EDGE,"E21.0.3.15"),sQuery(id+"F2.wireOp",EDGE,"E21.0.4.0"),sQuery(id+"F2.wireOp",EDGE,"E21.0.4.1"),sQuery(id+"F2.wireOp",EDGE,"E21.0.4.2"),sQuery(id+"F2.wireOp",EDGE,"E21.0.4.3"),sQuery(id+"F2.wireOp",EDGE,"E21.0.4.4"),sQuery(id+"F2.wireOp",EDGE,"E21.0.4.5"),sQuery(id+"F2.wireOp",EDGE,"E21.0.4.6"),sQuery(id+"F2.wireOp",EDGE,"E21.0.4.7"),sQuery(id+"F2.wireOp",EDGE,"E21.0.4.8"),sQuery(id+"F2.wireOp",EDGE,"E21.0.4.9"),sQuery(id+"F2.wireOp",EDGE,"E21.0.4.10"),sQuery(id+"F2.wireOp",EDGE,"E21.0.4.11"),sQuery(id+"F2.wireOp",EDGE,"E21.0.4.12"),sQuery(id+"F2.wireOp",EDGE,"E21.0.4.13"),sQuery(id+"F2.wireOp",EDGE,"E21.0.4.14"),sQuery(id+"F2.wireOp",EDGE,"E21.0.4.15"),sQuery(id+"F2.wireOp",EDGE,"E21.1.0.0"),sQuery(id+"F2.wireOp",EDGE,"E21.1.0.1"),sQuery(id+"F2.wireOp",EDGE,"E21.1.0.2"),sQuery(id+"F2.wireOp",EDGE,"E21.1.0.3"),sQuery(id+"F2.wireOp",EDGE,"E21.1.0.4"),sQuery(id+"F2.wireOp",EDGE,"E21.1.0.5"),sQuery(id+"F2.wireOp",EDGE,"E21.1.0.6"),sQuery(id+"F2.wireOp",EDGE,"E21.1.0.7"),sQuery(id+"F2.wireOp",EDGE,"E21.1.0.8"),sQuery(id+"F2.wireOp",EDGE,"E21.1.0.9"),sQuery(id+"F2.wireOp",EDGE,"E21.1.0.10"),sQuery(id+"F2.wireOp",EDGE,"E21.1.0.11"),sQuery(id+"F2.wireOp",EDGE,"E21.1.0.12"),sQuery(id+"F2.wireOp",EDGE,"E21.1.0.13"),sQuery(id+"F2.wireOp",EDGE,"E21.1.0.14"),sQuery(id+"F2.wireOp",EDGE,"E21.1.0.15"),sQuery(id+"F2.wireOp",EDGE,"E21.1.1.0"),sQuery(id+"F2.wireOp",EDGE,"E21.1.1.1"),sQuery(id+"F2.wireOp",EDGE,"E21.1.1.2"),sQuery(id+"F2.wireOp",EDGE,"E21.1.1.3"),sQuery(id+"F2.wireOp",EDGE,"E21.1.1.4"),sQuery(id+"F2.wireOp",EDGE,"E21.1.1.5"),sQuery(id+"F2.wireOp",EDGE,"E21.1.1.6"),sQuery(id+"F2.wireOp",EDGE,"E21.1.1.7"),sQuery(id+"F2.wireOp",EDGE,"E21.1.1.8"),sQuery(id+"F2.wireOp",EDGE,"E21.1.1.9"),sQuery(id+"F2.wireOp",EDGE,"E21.1.1.10"),sQuery(id+"F2.wireOp",EDGE,"E21.1.1.11"),sQuery(id+"F2.wireOp",EDGE,"E21.1.1.12"),sQuery(id+"F2.wireOp",EDGE,"E21.1.1.13"),sQuery(id+"F2.wireOp",EDGE,"E21.1.1.14"),sQuery(id+"F2.wireOp",EDGE,"E21.1.1.15"),sQuery(id+"F2.wireOp",EDGE,"E21.1.2.0"),sQuery(id+"F2.wireOp",EDGE,"E21.1.2.1"),sQuery(id+"F2.wireOp",EDGE,"E21.1.2.2"),sQuery(id+"F2.wireOp",EDGE,"E21.1.2.3"),sQuery(id+"F2.wireOp",EDGE,"E21.1.2.4"),sQuery(id+"F2.wireOp",EDGE,"E21.1.2.5"),sQuery(id+"F2.wireOp",EDGE,"E21.1.2.6"),sQuery(id+"F2.wireOp",EDGE,"E21.1.2.7"),sQuery(id+"F2.wireOp",EDGE,"E21.1.2.8"),sQuery(id+"F2.wireOp",EDGE,"E21.1.2.9"),sQuery(id+"F2.wireOp",EDGE,"E21.1.2.10"),sQuery(id+"F2.wireOp",EDGE,"E21.1.2.11"),sQuery(id+"F2.wireOp",EDGE,"E21.1.2.12"),sQuery(id+"F2.wireOp",EDGE,"E21.1.2.13"),sQuery(id+"F2.wireOp",EDGE,"E21.1.2.14"),sQuery(id+"F2.wireOp",EDGE,"E21.1.2.15"),sQuery(id+"F2.wireOp",EDGE,"E21.1.3.0"),sQuery(id+"F2.wireOp",EDGE,"E21.1.3.1"),sQuery(id+"F2.wireOp",EDGE,"E21.1.3.2"),sQuery(id+"F2.wireOp",EDGE,"E21.1.3.3"),sQuery(id+"F2.wireOp",EDGE,"E21.1.3.4"),sQuery(id+"F2.wireOp",EDGE,"E21.1.3.5"),sQuery(id+"F2.wireOp",EDGE,"E21.1.3.6"),sQuery(id+"F2.wireOp",EDGE,"E21.1.3.7"),sQuery(id+"F2.wireOp",EDGE,"E21.1.3.8"),sQuery(id+"F2.wireOp",EDGE,"E21.1.3.9"),sQuery(id+"F2.wireOp",EDGE,"E21.1.3.10"),sQuery(id+"F2.wireOp",EDGE,"E21.1.3.11"),sQuery(id+"F2.wireOp",EDGE,"E21.1.3.12"),sQuery(id+"F2.wireOp",EDGE,"E21.1.3.13"),sQuery(id+"F2.wireOp",EDGE,"E21.1.3.14"),sQuery(id+"F2.wireOp",EDGE,"E21.1.3.15"),sQuery(id+"F2.wireOp",EDGE,"E21.1.4.0"),sQuery(id+"F2.wireOp",EDGE,"E21.1.4.1"),sQuery(id+"F2.wireOp",EDGE,"E21.1.4.2"),sQuery(id+"F2.wireOp",EDGE,"E21.1.4.3"),sQuery(id+"F2.wireOp",EDGE,"E21.1.4.4"),sQuery(id+"F2.wireOp",EDGE,"E21.1.4.5"),sQuery(id+"F2.wireOp",EDGE,"E21.1.4.6"),sQuery(id+"F2.wireOp",EDGE,"E21.1.4.7"),sQuery(id+"F2.wireOp",EDGE,"E21.1.4.8"),sQuery(id+"F2.wireOp",EDGE,"E21.1.4.9"),sQuery(id+"F2.wireOp",EDGE,"E21.1.4.10"),sQuery(id+"F2.wireOp",EDGE,"E21.1.4.11"),sQuery(id+"F2.wireOp",EDGE,"E21.1.4.12"),sQuery(id+"F2.wireOp",EDGE,"E21.1.4.13"),sQuery(id+"F2.wireOp",EDGE,"E21.1.4.14"),sQuery(id+"F2.wireOp",EDGE,"E21.1.4.15"),sQuery(id+"F2.wireOp",EDGE,"E21.2.0.0"),sQuery(id+"F2.wireOp",EDGE,"E21.2.0.1"),sQuery(id+"F2.wireOp",EDGE,"E21.2.0.2"),sQuery(id+"F2.wireOp",EDGE,"E21.2.0.3"),sQuery(id+"F2.wireOp",EDGE,"E21.2.0.4"),sQuery(id+"F2.wireOp",EDGE,"E21.2.0.5"),sQuery(id+"F2.wireOp",EDGE,"E21.2.0.6"),sQuery(id+"F2.wireOp",EDGE,"E21.2.0.7"),sQuery(id+"F2.wireOp",EDGE,"E21.2.0.8"),sQuery(id+"F2.wireOp",EDGE,"E21.2.0.9"),sQuery(id+"F2.wireOp",EDGE,"E21.2.0.10"),sQuery(id+"F2.wireOp",EDGE,"E21.2.0.11"),sQuery(id+"F2.wireOp",EDGE,"E21.2.0.12"),sQuery(id+"F2.wireOp",EDGE,"E21.2.0.13"),sQuery(id+"F2.wireOp",EDGE,"E21.2.0.14"),sQuery(id+"F2.wireOp",EDGE,"E21.2.0.15"),sQuery(id+"F2.wireOp",EDGE,"E21.2.1.0"),sQuery(id+"F2.wireOp",EDGE,"E21.2.1.1"),sQuery(id+"F2.wireOp",EDGE,"E21.2.1.2"),sQuery(id+"F2.wireOp",EDGE,"E21.2.1.3"),sQuery(id+"F2.wireOp",EDGE,"E21.2.1.4"),sQuery(id+"F2.wireOp",EDGE,"E21.2.1.5"),sQuery(id+"F2.wireOp",EDGE,"E21.2.1.6"),sQuery(id+"F2.wireOp",EDGE,"E21.2.1.7"),sQuery(id+"F2.wireOp",EDGE,"E21.2.1.8"),sQuery(id+"F2.wireOp",EDGE,"E21.2.1.9"),sQuery(id+"F2.wireOp",EDGE,"E21.2.1.10"),sQuery(id+"F2.wireOp",EDGE,"E21.2.1.11"),sQuery(id+"F2.wireOp",EDGE,"E21.2.1.12"),sQuery(id+"F2.wireOp",EDGE,"E21.2.1.13"),sQuery(id+"F2.wireOp",EDGE,"E21.2.1.14"),sQuery(id+"F2.wireOp",EDGE,"E21.2.1.15"),sQuery(id+"F2.wireOp",EDGE,"E21.2.2.0"),sQuery(id+"F2.wireOp",EDGE,"E21.2.2.1"),sQuery(id+"F2.wireOp",EDGE,"E21.2.2.2"),sQuery(id+"F2.wireOp",EDGE,"E21.2.2.3"),sQuery(id+"F2.wireOp",EDGE,"E21.2.2.4"),sQuery(id+"F2.wireOp",EDGE,"E21.2.2.5"),sQuery(id+"F2.wireOp",EDGE,"E21.2.2.6"),sQuery(id+"F2.wireOp",EDGE,"E21.2.2.7"),sQuery(id+"F2.wireOp",EDGE,"E21.2.2.8"),sQuery(id+"F2.wireOp",EDGE,"E21.2.2.9"),sQuery(id+"F2.wireOp",EDGE,"E21.2.2.10"),sQuery(id+"F2.wireOp",EDGE,"E21.2.2.11"),sQuery(id+"F2.wireOp",EDGE,"E21.2.2.12"),sQuery(id+"F2.wireOp",EDGE,"E21.2.2.13"),sQuery(id+"F2.wireOp",EDGE,"E21.2.2.14"),sQuery(id+"F2.wireOp",EDGE,"E21.2.2.15"),sQuery(id+"F2.wireOp",EDGE,"E21.2.3.0"),sQuery(id+"F2.wireOp",EDGE,"E21.2.3.1"),sQuery(id+"F2.wireOp",EDGE,"E21.2.3.2"),sQuery(id+"F2.wireOp",EDGE,"E21.2.3.3"),sQuery(id+"F2.wireOp",EDGE,"E21.2.3.4"),sQuery(id+"F2.wireOp",EDGE,"E21.2.3.5"),sQuery(id+"F2.wireOp",EDGE,"E21.2.3.6"),sQuery(id+"F2.wireOp",EDGE,"E21.2.3.7"),sQuery(id+"F2.wireOp",EDGE,"E21.2.3.8"),sQuery(id+"F2.wireOp",EDGE,"E21.2.3.9"),sQuery(id+"F2.wireOp",EDGE,"E21.2.3.10"),sQuery(id+"F2.wireOp",EDGE,"E21.2.3.11"),sQuery(id+"F2.wireOp",EDGE,"E21.2.3.12"),sQuery(id+"F2.wireOp",EDGE,"E21.2.3.13"),sQuery(id+"F2.wireOp",EDGE,"E21.2.3.14"),sQuery(id+"F2.wireOp",EDGE,"E21.2.3.15"),sQuery(id+"F2.wireOp",EDGE,"E21.2.4.0"),sQuery(id+"F2.wireOp",EDGE,"E21.2.4.1"),sQuery(id+"F2.wireOp",EDGE,"E21.2.4.2"),sQuery(id+"F2.wireOp",EDGE,"E21.2.4.3"),sQuery(id+"F2.wireOp",EDGE,"E21.2.4.4"),sQuery(id+"F2.wireOp",EDGE,"E21.2.4.5"),sQuery(id+"F2.wireOp",EDGE,"E21.2.4.6"),sQuery(id+"F2.wireOp",EDGE,"E21.2.4.7"),sQuery(id+"F2.wireOp",EDGE,"E21.2.4.8"),sQuery(id+"F2.wireOp",EDGE,"E21.2.4.9"),sQuery(id+"F2.wireOp",EDGE,"E21.2.4.10"),sQuery(id+"F2.wireOp",EDGE,"E21.2.4.11"),sQuery(id+"F2.wireOp",EDGE,"E21.2.4.12"),sQuery(id+"F2.wireOp",EDGE,"E21.2.4.13"),sQuery(id+"F2.wireOp",EDGE,"E21.2.4.14"),sQuery(id+"F2.wireOp",EDGE,"E21.2.4.15")])],"isStart":false});
            var sketch = newSketch(context, id + "F4", { "sketchPlane" : qUnion([Q0])});
            skLineSegment(sketch, "E23.bottom", {"start": v(-6.5, 50) * mm, "end": v(-3.5, 50) * mm});
            skLineSegment(sketch, "E23.top", {"start": v(-6.5, 36) * mm, "end": v(-3.5, 36) * mm});
            skLineSegment(sketch, "E23.left", {"start": v(-6.5, 50) * mm, "end": v(-6.5, 36) * mm});
            skLineSegment(sketch, "E23.right", {"start": v(-3.5, 50) * mm, "end": v(-3.5, 36) * mm});
            skLineSegment(sketch, "E24.bottom", {"start": v(-6.5, 13) * mm, "end": v(-3.5, 13) * mm});
            skLineSegment(sketch, "E24.top", {"start": v(-6.5, -1) * mm, "end": v(-3.5, -1) * mm});
            skLineSegment(sketch, "E24.left", {"start": v(-6.5, 13) * mm, "end": v(-6.5, -1) * mm});
            skLineSegment(sketch, "E24.right", {"start": v(-3.5, 13) * mm, "end": v(-3.5, -1) * mm});
            skLineSegment(sketch, "E25.bottom", {"start": v(150.7, 50) * mm, "end": v(153.7, 50) * mm});
            skLineSegment(sketch, "E25.top", {"start": v(150.7, 36) * mm, "end": v(153.7, 36) * mm});
            skLineSegment(sketch, "E25.left", {"start": v(150.7, 50) * mm, "end": v(150.7, 36) * mm});
            skLineSegment(sketch, "E25.right", {"start": v(153.7, 50) * mm, "end": v(153.7, 36) * mm});
            skLineSegment(sketch, "E26.bottom", {"start": v(-10, 33.5) * mm, "end": v(-6.5, 33.5) * mm});
            skLineSegment(sketch, "E26.top", {"start": v(-10, 15.5) * mm, "end": v(-6.5, 15.5) * mm});
            skLineSegment(sketch, "E26.left", {"start": v(-10, 33.5) * mm, "end": v(-10, 15.5) * mm});
            skLineSegment(sketch, "E26.right", {"start": v(-6.5, 33.5) * mm, "end": v(-6.5, 15.5) * mm});
            skLineSegment(sketch, "E27.bottom", {"start": v(157.2, 33.5) * mm, "end": v(153.7, 33.5) * mm});
            skLineSegment(sketch, "E27.top", {"start": v(157.2, 15.5) * mm, "end": v(153.7, 15.5) * mm});
            skLineSegment(sketch, "E27.left", {"start": v(157.2, 33.5) * mm, "end": v(157.2, 15.5) * mm});
            skLineSegment(sketch, "E27.right", {"start": v(153.7, 33.5) * mm, "end": v(153.7, 15.5) * mm});
            skLineSegment(sketch, "E28", {"start": v(-6.5, 24.5) * mm, "end": v(2, 24.5) * mm, "construction": true});
            skLineSegment(sketch, "E29", {"start": v(-10, 57) * mm, "end": v(-6.5, 50) * mm, "construction": true});
            skLineSegment(sketch, "E30", {"start": v(-6.5, 36) * mm, "end": v(-6.5, 33.5) * mm, "construction": true});
            skLineSegment(sketch, "E31", {"start": v(-6.5, 15.5) * mm, "end": v(-6.5, 13) * mm, "construction": true});
            skLineSegment(sketch, "E32", {"start": v(-6.5, -1) * mm, "end": v(-10, -8) * mm, "construction": true});
            skLineSegment(sketch, "E33.bottom", {"start": v(8.85, 57) * mm, "end": v(26.85, 57) * mm});
            skLineSegment(sketch, "E33.top", {"start": v(8.85, 53.5) * mm, "end": v(26.85, 53.5) * mm});
            skLineSegment(sketch, "E33.left", {"start": v(8.85, 57) * mm, "end": v(8.85, 53.5) * mm});
            skLineSegment(sketch, "E33.right", {"start": v(26.85, 57) * mm, "end": v(26.85, 53.5) * mm});
            skLineSegment(sketch, "E34.bottom", {"start": v(46.02, 57) * mm, "end": v(64.02, 57) * mm});
            skLineSegment(sketch, "E34.top", {"start": v(46.02, 53.5) * mm, "end": v(64.02, 53.5) * mm});
            skLineSegment(sketch, "E34.left", {"start": v(46.02, 57) * mm, "end": v(46.02, 53.5) * mm});
            skLineSegment(sketch, "E34.right", {"start": v(64.02, 57) * mm, "end": v(64.02, 53.5) * mm});
            skLineSegment(sketch, "E35.bottom", {"start": v(83.18, 57) * mm, "end": v(101.18, 57) * mm});
            skLineSegment(sketch, "E35.top", {"start": v(83.18, 53.5) * mm, "end": v(101.18, 53.5) * mm});
            skLineSegment(sketch, "E35.left", {"start": v(83.18, 57) * mm, "end": v(83.18, 53.5) * mm});
            skLineSegment(sketch, "E35.right", {"start": v(101.18, 57) * mm, "end": v(101.18, 53.5) * mm});
            skLineSegment(sketch, "E36.bottom", {"start": v(120.35, 57) * mm, "end": v(138.35, 57) * mm});
            skLineSegment(sketch, "E36.top", {"start": v(120.35, 53.5) * mm, "end": v(138.35, 53.5) * mm});
            skLineSegment(sketch, "E36.left", {"start": v(120.35, 57) * mm, "end": v(120.35, 53.5) * mm});
            skLineSegment(sketch, "E36.right", {"start": v(138.35, 57) * mm, "end": v(138.35, 53.5) * mm});
            skLineSegment(sketch, "E37", {"start": v(-10, 57) * mm, "end": v(8.85, 53.5) * mm, "construction": true});
            skLineSegment(sketch, "E38", {"start": v(26.85, 53.5) * mm, "end": v(46.02, 53.5) * mm, "construction": true});
            skLineSegment(sketch, "E39", {"start": v(64.02, 53.5) * mm, "end": v(83.18, 53.5) * mm, "construction": true});
            skLineSegment(sketch, "E40", {"start": v(101.18, 53.5) * mm, "end": v(120.35, 53.5) * mm, "construction": true});
            skLineSegment(sketch, "E41", {"start": v(138.35, 53.5) * mm, "end": v(157.2, 57) * mm, "construction": true});
            skLineSegment(sketch, "E42.bottom", {"start": v(-10, -8) * mm, "end": v(8.85, -8) * mm});
            skLineSegment(sketch, "E42.top", {"start": v(-10, -4.5) * mm, "end": v(8.85, -4.5) * mm});
            skLineSegment(sketch, "E42.left", {"start": v(-10, -8) * mm, "end": v(-10, -4.5) * mm});
            skLineSegment(sketch, "E42.right", {"start": v(8.85, -8) * mm, "end": v(8.85, -4.5) * mm});
            skLineSegment(sketch, "E43.bottom", {"start": v(26.85, -4.5) * mm, "end": v(46.02, -4.5) * mm});
            skLineSegment(sketch, "E43.top", {"start": v(26.85, -8) * mm, "end": v(46.02, -8) * mm});
            skLineSegment(sketch, "E43.left", {"start": v(26.85, -4.5) * mm, "end": v(26.85, -8) * mm});
            skLineSegment(sketch, "E43.right", {"start": v(46.02, -4.5) * mm, "end": v(46.02, -8) * mm});
            skLineSegment(sketch, "E44.bottom", {"start": v(64.02, -4.5) * mm, "end": v(83.18, -4.5) * mm});
            skLineSegment(sketch, "E44.top", {"start": v(64.02, -8) * mm, "end": v(83.18, -8) * mm});
            skLineSegment(sketch, "E44.left", {"start": v(64.02, -4.5) * mm, "end": v(64.02, -8) * mm});
            skLineSegment(sketch, "E44.right", {"start": v(83.18, -4.5) * mm, "end": v(83.18, -8) * mm});
            skLineSegment(sketch, "E45.bottom", {"start": v(101.18, -4.5) * mm, "end": v(120.35, -4.5) * mm});
            skLineSegment(sketch, "E45.top", {"start": v(101.18, -8) * mm, "end": v(120.35, -8) * mm});
            skLineSegment(sketch, "E45.left", {"start": v(101.18, -4.5) * mm, "end": v(101.18, -8) * mm});
            skLineSegment(sketch, "E45.right", {"start": v(120.35, -4.5) * mm, "end": v(120.35, -8) * mm});
            skLineSegment(sketch, "E46.bottom", {"start": v(138.35, -4.5) * mm, "end": v(157.2, -4.5) * mm});
            skLineSegment(sketch, "E46.top", {"start": v(138.35, -8) * mm, "end": v(157.2, -8) * mm});
            skLineSegment(sketch, "E46.left", {"start": v(138.35, -4.5) * mm, "end": v(138.35, -8) * mm});
            skLineSegment(sketch, "E46.right", {"start": v(157.2, -4.5) * mm, "end": v(157.2, -8) * mm});
            skLineSegment(sketch, "E47.bottom", {"start": v(150.7, 13) * mm, "end": v(153.7, 13) * mm});
            skLineSegment(sketch, "E47.top", {"start": v(150.7, -1) * mm, "end": v(153.7, -1) * mm});
            skLineSegment(sketch, "E47.left", {"start": v(150.7, 13) * mm, "end": v(150.7, -1) * mm});
            skLineSegment(sketch, "E47.right", {"start": v(153.7, 13) * mm, "end": v(153.7, -1) * mm});
            skSolve(sketch);
        }
        {
            var Q0;
            Q0 = qSketchRegion(id + "F4", true);
            extrude(context, id + "F5", {"entities" : qUnion([Q0]), "operationType" : NewBodyOperationType.REMOVE, "oppositeDirection" : true, "depth" : 25 * mm, "offsetDistance" : 25 * mm});
        }
        {
            var Q0;
            Q0=makeQuery(id+"F5.boolean.opBoolean","COPY",FACE,{"derivedFrom":makeQuery(id+"F5.opExtrude","SWEPT_FACE",FACE,{"disambiguationData":[OSD([sQuery(id+"F4.wireOp",EDGE,"E47.left")])]})});
            var sketch = newSketch(context, id + "F6", { "sketchPlane" : qUnion([Q0])});
            skLineSegment(sketch, "E48", {"start": v(-1, -8.5) * mm, "end": v(-1, 6.5) * mm});
            skLineSegment(sketch, "E49", {"start": v(-1, 6.5) * mm, "end": v(13, 6.5) * mm});
            skLineSegment(sketch, "E50", {"start": v(13, 6.5) * mm, "end": v(13, 3) * mm});
            skLineSegment(sketch, "E51", {"start": v(13, 3) * mm, "end": v(36, 3) * mm});
            skLineSegment(sketch, "E52", {"start": v(36, 3) * mm, "end": v(36, 6.5) * mm});
            skLineSegment(sketch, "E53", {"start": v(36, 6.5) * mm, "end": v(50, 6.5) * mm});
            skLineSegment(sketch, "E54", {"start": v(50, 6.5) * mm, "end": v(50, -8.5) * mm});
            skLineSegment(sketch, "E55", {"start": v(50, -8.5) * mm, "end": v(44.34, -8.5) * mm});
            skLineSegment(sketch, "E56", {"start": v(44.34, -8.5) * mm, "end": v(37.84, -2) * mm});
            skLineSegment(sketch, "E57", {"start": v(4.66, -8.5) * mm, "end": v(11.16, -2) * mm});
            skLineSegment(sketch, "E58", {"start": v(4.66, -8.5) * mm, "end": v(-1, -8.5) * mm});
            skCircle(sketch, "E59", {"center": v(3, -4.5) * mm, "radius": 1.75 * mm});
            skLineSegment(sketch, "E60", {"start": v(-4.5, 3) * mm, "end": v(3, -4.5) * mm, "construction": true});
            skLineSegment(sketch, "E61", {"start": v(11.16, -2) * mm, "end": v(37.84, -2) * mm});
            skCircle(sketch, "E62", {"center": v(46, -4.5) * mm, "radius": 1.75 * mm});
            skSolve(sketch);
        }
        {
            var Q0;
            Q0 = qSketchRegion(id + "F6", true);
            extrude(context, id + "F7", {"entities" : qUnion([Q0]), "depth" : 3 * mm, "offsetDistance" : 25 * mm});
        }
        {
            var Q0;
            Q0=makeQuery(id+"F7.opExtrude","SWEPT_EDGE",EDGE,{"disambiguationData":[OSD([sQuery(id+"F6.wireOp",EDGE,"E48"),sQuery(id+"F6.wireOp",EDGE,"E58")])]});
            var Q1;
            Q1=makeQuery(id+"F7.opExtrude","SWEPT_EDGE",EDGE,{"disambiguationData":[OSD([sQuery(id+"F6.wireOp",EDGE,"E57"),sQuery(id+"F6.wireOp",EDGE,"E58")])]});
            var Q2;
            Q2=makeQuery(id+"F7.opExtrude","SWEPT_EDGE",EDGE,{"disambiguationData":[OSD([sQuery(id+"F6.wireOp",EDGE,"E57"),sQuery(id+"F6.wireOp",EDGE,"E61")])]});
            var Q3;
            Q3=makeQuery(id+"F7.opExtrude","SWEPT_EDGE",EDGE,{"disambiguationData":[OSD([sQuery(id+"F6.wireOp",EDGE,"E56"),sQuery(id+"F6.wireOp",EDGE,"E61")])]});
            var Q4;
            Q4=makeQuery(id+"F7.opExtrude","SWEPT_EDGE",EDGE,{"disambiguationData":[OSD([sQuery(id+"F6.wireOp",EDGE,"E55"),sQuery(id+"F6.wireOp",EDGE,"E56")])]});
            var Q5;
            Q5=makeQuery(id+"F7.opExtrude","SWEPT_EDGE",EDGE,{"disambiguationData":[OSD([sQuery(id+"F6.wireOp",EDGE,"E54"),sQuery(id+"F6.wireOp",EDGE,"E55")])]});
            fillet(context, id + "F8", {"entities" : qUnion([Q0, Q1, Q2, Q3, Q4, Q5]), "radius" : 4 * mm, "tangentPropagation" : true, "allowEdgeOverflow" : false});
        }
    });
